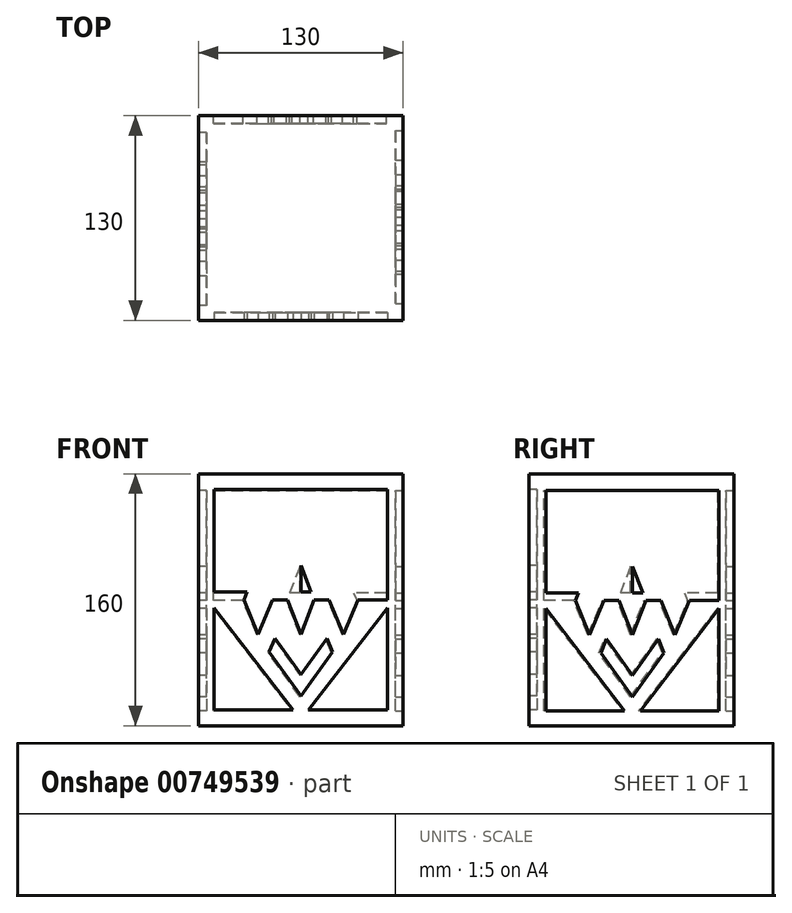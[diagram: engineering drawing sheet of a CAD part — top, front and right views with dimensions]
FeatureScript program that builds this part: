
annotation { "Feature Type Name" : "Feature", "Feature Type Description" : "" }
export const myFeature = defineFeature(function(context is Context, id is Id, definition is map)
    precondition{}
    {
        {
            var Q0;
            Q0=qCreatedBy(makeId("Top.planeOp"),FACE);
            var sketch = newSketch(context, id + "F0", { "sketchPlane" : qUnion([Q0])});
            skLineSegment(sketch, "E0.bottom", {"start": v(0, 0) * mm, "end": v(130, 0) * mm});
            skLineSegment(sketch, "E0.top", {"start": v(0, 130) * mm, "end": v(130, 130) * mm});
            skLineSegment(sketch, "E0.left", {"start": v(0, 0) * mm, "end": v(0, 130) * mm});
            skLineSegment(sketch, "E0.right", {"start": v(130, 0) * mm, "end": v(130, 130) * mm});
            skSolve(sketch);
        }
        {
            var Q0;
            Q0=makeQuery(id+"F0.imprint","IMPRINT",FACE,{"disambiguationData":[TD([[makeQuery(id+"F0.imprint","IMPRINT",EDGE,{"derivedFrom":sQuery(id+"F0.wireOp",EDGE,"E0.bottom")}),1.0]])]});
            extrude(context, id + "F1", {"entities" : qUnion([Q0]), "depth" : 160 * mm, "offsetDistance" : 25 * mm});
        }
        {
            var Q0;
            Q0=makeQuery(id+"F1.opExtrude","SWEPT_FACE",FACE,{"disambiguationData":[OSD([sQuery(id+"F0.wireOp",EDGE,"E0.bottom")])]});
            var sketch = newSketch(context, id + "F2", { "sketchPlane" : qUnion([Q0])});
            skLineSegment(sketch, "E1.0", {"start": v(10, 10) * mm, "end": v(120, 10) * mm});
            skLineSegment(sketch, "E1.1", {"start": v(10, 150) * mm, "end": v(10, 10) * mm});
            skLineSegment(sketch, "E1.2", {"start": v(120, 150) * mm, "end": v(10, 150) * mm});
            skLineSegment(sketch, "E1.3", {"start": v(120, 10) * mm, "end": v(120, 150) * mm});
            skLineSegment(sketch, "E2", {"start": v(10, 80) * mm, "end": v(120, 80) * mm});
            skLineSegment(sketch, "E3.0", {"start": v(10, 75) * mm, "end": v(120, 75) * mm});
            skLineSegment(sketch, "E4.0", {"start": v(10, 85) * mm, "end": v(120, 85) * mm});
            skLineSegment(sketch, "E5", {"start": v(10, 85) * mm, "end": v(60, 150) * mm});
            skLineSegment(sketch, "E6", {"start": v(65, 141.04) * mm, "end": v(44.9, 113.15) * mm});
            skLineSegment(sketch, "E7", {"start": v(44.9, 113.15) * mm, "end": v(48.52, 104.4) * mm});
            skLineSegment(sketch, "E8", {"start": v(48.52, 104.4) * mm, "end": v(65, 127.47) * mm});
            skLineSegment(sketch, "E9", {"start": v(47.01, 80) * mm, "end": v(28.77, 80) * mm});
            skLineSegment(sketch, "E10", {"start": v(37.89, 80) * mm, "end": v(37.89, 101.84) * mm});
            skLineSegment(sketch, "E11", {"start": v(37.89, 101.84) * mm, "end": v(28.77, 80) * mm});
            skLineSegment(sketch, "E12", {"start": v(37.89, 101.84) * mm, "end": v(47.01, 80) * mm});
            skLineSegment(sketch, "E13", {"start": v(65, 80) * mm, "end": v(65, 101.84) * mm});
            skLineSegment(sketch, "E14", {"start": v(65, 101.84) * mm, "end": v(56.51, 80) * mm});
            skLineSegment(sketch, "E15.MirrorCS", {"start": v(65, 141.04) * mm, "end": v(85.1, 113.15) * mm});
            skLineSegment(sketch, "E16.MirrorCS", {"start": v(81.48, 104.4) * mm, "end": v(65, 127.47) * mm});
            skLineSegment(sketch, "E17.MirrorCS", {"start": v(85.1, 113.15) * mm, "end": v(81.48, 104.4) * mm});
            skLineSegment(sketch, "E18.MirrorCS", {"start": v(120, 85) * mm, "end": v(70, 150) * mm});
            skLineSegment(sketch, "E19.MirrorCS", {"start": v(92.11, 101.84) * mm, "end": v(82.99, 80) * mm});
            skLineSegment(sketch, "E20.MirrorCS", {"start": v(92.11, 80) * mm, "end": v(92.11, 101.84) * mm});
            skLineSegment(sketch, "E21.MirrorCS", {"start": v(92.11, 101.84) * mm, "end": v(101.23, 80) * mm});
            skLineSegment(sketch, "E22.MirrorCS", {"start": v(65, 101.84) * mm, "end": v(73.49, 80) * mm});
            skLineSegment(sketch, "E23.MirrorCS", {"start": v(120, 75) * mm, "end": v(70, 10) * mm});
            skLineSegment(sketch, "E24.MirrorCS", {"start": v(92.11, 58.16) * mm, "end": v(101.23, 80) * mm});
            skLineSegment(sketch, "E25.MirrorCS", {"start": v(92.11, 80) * mm, "end": v(92.11, 58.16) * mm});
            skLineSegment(sketch, "E26.MirrorCS", {"start": v(92.11, 58.16) * mm, "end": v(82.99, 80) * mm});
            skLineSegment(sketch, "E27.MirrorCS", {"start": v(81.48, 55.6) * mm, "end": v(65, 32.53) * mm});
            skLineSegment(sketch, "E28.MirrorCS", {"start": v(85.1, 46.85) * mm, "end": v(81.48, 55.6) * mm});
            skLineSegment(sketch, "E29.MirrorCS", {"start": v(65, 18.96) * mm, "end": v(85.1, 46.85) * mm});
            skLineSegment(sketch, "E30.MirrorCS", {"start": v(65, 18.96) * mm, "end": v(44.9, 46.85) * mm});
            skLineSegment(sketch, "E31.MirrorCS", {"start": v(48.52, 55.6) * mm, "end": v(65, 32.53) * mm});
            skLineSegment(sketch, "E32.MirrorCS", {"start": v(44.9, 46.85) * mm, "end": v(48.52, 55.6) * mm});
            skLineSegment(sketch, "E33.MirrorCS", {"start": v(65, 58.16) * mm, "end": v(56.51, 80) * mm});
            skLineSegment(sketch, "E34.MirrorCS", {"start": v(65, 58.16) * mm, "end": v(73.49, 80) * mm});
            skLineSegment(sketch, "E35.MirrorCS", {"start": v(37.89, 58.16) * mm, "end": v(47.01, 80) * mm});
            skLineSegment(sketch, "E36.MirrorCS", {"start": v(37.89, 58.16) * mm, "end": v(28.77, 80) * mm});
            skLineSegment(sketch, "E37.MirrorCS", {"start": v(10, 75) * mm, "end": v(60, 10) * mm});
            skLineSegment(sketch, "E38", {"start": v(10, 150) * mm, "end": v(10, 85) * mm});
            skLineSegment(sketch, "E39", {"start": v(10, 150) * mm, "end": v(120, 150) * mm});
            skLineSegment(sketch, "E40", {"start": v(120, 150) * mm, "end": v(120, 10) * mm});
            skLineSegment(sketch, "E41", {"start": v(120, 10) * mm, "end": v(10, 10) * mm});
            skLineSegment(sketch, "E42", {"start": v(10, 10) * mm, "end": v(10, 75) * mm});
            skLineSegment(sketch, "E43.trimOffspring", {"start": v(60, 88.97) * mm, "end": v(60, 71.03) * mm});
            skLineSegment(sketch, "E44.trimOffspring", {"start": v(65, 101.84) * mm, "end": v(65, 58.16) * mm});
            skLineSegment(sketch, "E45.trimOffspring", {"start": v(65, 18.96) * mm, "end": v(65, 10) * mm});
            skPoint(sketch, "E46.start.orphan", {"position": v(65, 150) * mm});
            skSolve(sketch);
        }
        {
            var Q0;
            Q0=makeQuery(id+"F2.imprint","IMPRINT",FACE,{"disambiguationData":[TD([[makeQuery(id+"F2.imprint","IMPRINT",EDGE,{"derivedFrom":sQuery(id+"F2.wireOp",EDGE,"E6")}),1.0]])]});
            var Q1;
            Q1=makeQuery(id+"F2.imprint","IMPRINT",FACE,{"disambiguationData":[TD([[makeQuery(id+"F2.imprint","IMPRINT",EDGE,{"derivedFrom":sQuery(id+"F2.wireOp",EDGE,"E27.MirrorCS")}),1.0]])]});
            var Q2;
            {var subQ0=sQuery(id+"F2.wireOp",EDGE,"E23.MirrorCS");Q2=makeQuery(id+"F2.imprint","IMPRINT",FACE,{"disambiguationData":[TD([[makeQuery(id+"F2.imprint","IMPRINT",EDGE,{"derivedFrom":subQ0}),1.0]])]});}
            var Q3;
            {var subQ0=sQuery(id+"F2.wireOp",EDGE,"E37.MirrorCS");Q3=makeQuery(id+"F2.imprint","IMPRINT",FACE,{"disambiguationData":[TD([[makeQuery(id+"F2.imprint","IMPRINT",EDGE,{"derivedFrom":subQ0}),-1.0]])]});}
            var Q4;
            {var subQ0=sQuery(id+"F2.wireOp",EDGE,"E5");Q4=makeQuery(id+"F2.imprint","IMPRINT",FACE,{"disambiguationData":[TD([[makeQuery(id+"F2.imprint","IMPRINT",EDGE,{"derivedFrom":subQ0}),1.0]])]});}
            var Q5;
            {var subQ0=sQuery(id+"F2.wireOp",EDGE,"E18.MirrorCS");Q5=makeQuery(id+"F2.imprint","IMPRINT",FACE,{"disambiguationData":[TD([[makeQuery(id+"F2.imprint","IMPRINT",EDGE,{"derivedFrom":subQ0}),-1.0]])]});}
            var Q6;
            {var subQ0=sQuery(id+"F2.wireOp",EDGE,"E20.MirrorCS");var subQ1=sQuery(id+"F2.wireOp",EDGE,"E4.0");var subQ2=makeQuery(id+"F2.imprint","INTERSECT",VERTEX,{"derivedFrom":[subQ1,subQ0]});Q6=makeQuery(id+"F2.imprint","IMPRINT",FACE,{"disambiguationData":[TD([[makeQuery(id+"F2.imprint","IMPRINT",EDGE,{"disambiguationData":[TD([[subQ2,-1.0]])],"derivedFrom":subQ1}),1.0]])]});}
            var Q7;
            {var subQ0=sQuery(id+"F2.wireOp",EDGE,"E19.MirrorCS");var subQ1=sQuery(id+"F2.wireOp",EDGE,"E4.0");var subQ2=makeQuery(id+"F2.imprint","INTERSECT",VERTEX,{"derivedFrom":[subQ1,subQ0]});Q7=makeQuery(id+"F2.imprint","IMPRINT",FACE,{"disambiguationData":[TD([[makeQuery(id+"F2.imprint","IMPRINT",EDGE,{"disambiguationData":[TD([[subQ2,-1.0]])],"derivedFrom":subQ1}),1.0]])]});}
            var Q8;
            {var subQ0=sQuery(id+"F2.wireOp",EDGE,"E19.MirrorCS");var subQ5=sQuery(id+"F2.wireOp",EDGE,"E4.0");var subQ6=makeQuery(id+"F2.imprint","INTERSECT",VERTEX,{"derivedFrom":[subQ5,subQ0]});Q8=makeQuery(id+"F2.imprint","IMPRINT",FACE,{"disambiguationData":[TD([[makeQuery(id+"F2.imprint","IMPRINT",EDGE,{"disambiguationData":[TD([[subQ6,-1.0]])],"derivedFrom":subQ5}),-1.0]])]});}
            var Q9;
            {var subQ3=sQuery(id+"F2.wireOp",EDGE,"E20.MirrorCS");var subQ5=sQuery(id+"F2.wireOp",EDGE,"E4.0");var subQ7=makeQuery(id+"F2.imprint","INTERSECT",VERTEX,{"derivedFrom":[subQ5,subQ3]});Q9=makeQuery(id+"F2.imprint","IMPRINT",FACE,{"disambiguationData":[TD([[makeQuery(id+"F2.imprint","IMPRINT",EDGE,{"disambiguationData":[TD([[subQ7,-1.0]])],"derivedFrom":subQ5}),-1.0]])]});}
            var Q10;
            {var subQ3=sQuery(id+"F2.wireOp",EDGE,"E25.MirrorCS");var subQ5=sQuery(id+"F2.wireOp",EDGE,"E3.0");var subQ6=makeQuery(id+"F2.imprint","INTERSECT",VERTEX,{"derivedFrom":[subQ5,subQ3]});Q10=makeQuery(id+"F2.imprint","IMPRINT",FACE,{"disambiguationData":[TD([[makeQuery(id+"F2.imprint","IMPRINT",EDGE,{"disambiguationData":[TD([[subQ6,-1.0]])],"derivedFrom":subQ5}),1.0]])]});}
            var Q11;
            {var subQ0=sQuery(id+"F2.wireOp",EDGE,"E26.MirrorCS");var subQ5=sQuery(id+"F2.wireOp",EDGE,"E3.0");var subQ6=makeQuery(id+"F2.imprint","INTERSECT",VERTEX,{"derivedFrom":[subQ5,subQ0]});Q11=makeQuery(id+"F2.imprint","IMPRINT",FACE,{"disambiguationData":[TD([[makeQuery(id+"F2.imprint","IMPRINT",EDGE,{"disambiguationData":[TD([[subQ6,-1.0]])],"derivedFrom":subQ5}),1.0]])]});}
            var Q12;
            {var subQ0=sQuery(id+"F2.wireOp",EDGE,"E26.MirrorCS");var subQ1=sQuery(id+"F2.wireOp",EDGE,"E3.0");var subQ2=makeQuery(id+"F2.imprint","INTERSECT",VERTEX,{"derivedFrom":[subQ1,subQ0]});Q12=makeQuery(id+"F2.imprint","IMPRINT",FACE,{"disambiguationData":[TD([[makeQuery(id+"F2.imprint","IMPRINT",EDGE,{"disambiguationData":[TD([[subQ2,-1.0]])],"derivedFrom":subQ1}),-1.0]])]});}
            var Q13;
            {var subQ0=sQuery(id+"F2.wireOp",EDGE,"E25.MirrorCS");var subQ1=sQuery(id+"F2.wireOp",EDGE,"E3.0");var subQ2=makeQuery(id+"F2.imprint","INTERSECT",VERTEX,{"derivedFrom":[subQ1,subQ0]});Q13=makeQuery(id+"F2.imprint","IMPRINT",FACE,{"disambiguationData":[TD([[makeQuery(id+"F2.imprint","IMPRINT",EDGE,{"disambiguationData":[TD([[subQ2,-1.0]])],"derivedFrom":subQ1}),-1.0]])]});}
            var Q14;
            {var subQ0=sQuery(id+"F2.wireOp",EDGE,"E44.trimOffspring");var subQ1=sQuery(id+"F2.wireOp",EDGE,"E4.0");var subQ2=makeQuery(id+"F2.imprint","INTERSECT",VERTEX,{"derivedFrom":[subQ1,subQ0]});Q14=makeQuery(id+"F2.imprint","IMPRINT",FACE,{"disambiguationData":[TD([[makeQuery(id+"F2.imprint","IMPRINT",EDGE,{"disambiguationData":[TD([[subQ2,-1.0]])],"derivedFrom":subQ1}),1.0]])]});}
            var Q15;
            {var subQ0=sQuery(id+"F2.wireOp",EDGE,"E43.trimOffspring");var subQ1=sQuery(id+"F2.wireOp",EDGE,"E4.0");var subQ2=makeQuery(id+"F2.imprint","INTERSECT",VERTEX,{"derivedFrom":[subQ1,subQ0]});Q15=makeQuery(id+"F2.imprint","IMPRINT",FACE,{"disambiguationData":[TD([[makeQuery(id+"F2.imprint","IMPRINT",EDGE,{"disambiguationData":[TD([[subQ2,-1.0]])],"derivedFrom":subQ1}),1.0]])]});}
            var Q16;
            {var subQ0=sQuery(id+"F2.wireOp",EDGE,"E14");var subQ1=sQuery(id+"F2.wireOp",EDGE,"E4.0");var subQ2=makeQuery(id+"F2.imprint","INTERSECT",VERTEX,{"derivedFrom":[subQ1,subQ0]});Q16=makeQuery(id+"F2.imprint","IMPRINT",FACE,{"disambiguationData":[TD([[makeQuery(id+"F2.imprint","IMPRINT",EDGE,{"disambiguationData":[TD([[subQ2,-1.0]])],"derivedFrom":subQ1}),1.0]])]});}
            var Q17;
            {var subQ0=sQuery(id+"F2.wireOp",EDGE,"E14");var subQ5=sQuery(id+"F2.wireOp",EDGE,"E4.0");var subQ6=makeQuery(id+"F2.imprint","INTERSECT",VERTEX,{"derivedFrom":[subQ5,subQ0]});Q17=makeQuery(id+"F2.imprint","IMPRINT",FACE,{"disambiguationData":[TD([[makeQuery(id+"F2.imprint","IMPRINT",EDGE,{"disambiguationData":[TD([[subQ6,-1.0]])],"derivedFrom":subQ5}),-1.0]])]});}
            var Q18;
            {var subQ0=sQuery(id+"F2.wireOp",EDGE,"E33.MirrorCS");var subQ5=sQuery(id+"F2.wireOp",EDGE,"E3.0");var subQ6=makeQuery(id+"F2.imprint","INTERSECT",VERTEX,{"derivedFrom":[subQ5,subQ0]});Q18=makeQuery(id+"F2.imprint","IMPRINT",FACE,{"disambiguationData":[TD([[makeQuery(id+"F2.imprint","IMPRINT",EDGE,{"disambiguationData":[TD([[subQ6,-1.0]])],"derivedFrom":subQ5}),1.0]])]});}
            var Q19;
            {var subQ0=sQuery(id+"F2.wireOp",EDGE,"E43.trimOffspring");var subQ1=sQuery(id+"F2.wireOp",EDGE,"E2");var subQ2=makeQuery(id+"F2.imprint","INTERSECT",VERTEX,{"derivedFrom":[subQ1,subQ0]});Q19=makeQuery(id+"F2.imprint","IMPRINT",FACE,{"disambiguationData":[TD([[makeQuery(id+"F2.imprint","IMPRINT",EDGE,{"disambiguationData":[TD([[subQ2,-1.0]])],"derivedFrom":subQ1}),1.0]])]});}
            var Q20;
            {var subQ0=sQuery(id+"F2.wireOp",EDGE,"E43.trimOffspring");var subQ1=sQuery(id+"F2.wireOp",EDGE,"E2");var subQ2=makeQuery(id+"F2.imprint","INTERSECT",VERTEX,{"derivedFrom":[subQ1,subQ0]});Q20=makeQuery(id+"F2.imprint","IMPRINT",FACE,{"disambiguationData":[TD([[makeQuery(id+"F2.imprint","IMPRINT",EDGE,{"disambiguationData":[TD([[subQ2,-1.0]])],"derivedFrom":subQ1}),-1.0]])]});}
            var Q21;
            {var subQ0=sQuery(id+"F2.wireOp",EDGE,"E43.trimOffspring");var subQ1=sQuery(id+"F2.wireOp",EDGE,"E3.0");var subQ2=makeQuery(id+"F2.imprint","INTERSECT",VERTEX,{"derivedFrom":[subQ1,subQ0]});Q21=makeQuery(id+"F2.imprint","IMPRINT",FACE,{"disambiguationData":[TD([[makeQuery(id+"F2.imprint","IMPRINT",EDGE,{"disambiguationData":[TD([[subQ2,-1.0]])],"derivedFrom":subQ1}),-1.0]])]});}
            var Q22;
            {var subQ0=sQuery(id+"F2.wireOp",EDGE,"E44.trimOffspring");var subQ1=sQuery(id+"F2.wireOp",EDGE,"E3.0");var subQ2=makeQuery(id+"F2.imprint","INTERSECT",VERTEX,{"derivedFrom":[subQ1,subQ0]});Q22=makeQuery(id+"F2.imprint","IMPRINT",FACE,{"disambiguationData":[TD([[makeQuery(id+"F2.imprint","IMPRINT",EDGE,{"disambiguationData":[TD([[subQ2,-1.0]])],"derivedFrom":subQ1}),-1.0]])]});}
            var Q23;
            {var subQ3=sQuery(id+"F2.wireOp",EDGE,"E44.trimOffspring");var subQ5=sQuery(id+"F2.wireOp",EDGE,"E3.0");var subQ6=makeQuery(id+"F2.imprint","INTERSECT",VERTEX,{"derivedFrom":[subQ5,subQ3]});Q23=makeQuery(id+"F2.imprint","IMPRINT",FACE,{"disambiguationData":[TD([[makeQuery(id+"F2.imprint","IMPRINT",EDGE,{"disambiguationData":[TD([[subQ6,-1.0]])],"derivedFrom":subQ5}),1.0]])]});}
            var Q24;
            {var subQ3=sQuery(id+"F2.wireOp",EDGE,"E44.trimOffspring");var subQ5=sQuery(id+"F2.wireOp",EDGE,"E4.0");var subQ6=makeQuery(id+"F2.imprint","INTERSECT",VERTEX,{"derivedFrom":[subQ5,subQ3]});Q24=makeQuery(id+"F2.imprint","IMPRINT",FACE,{"disambiguationData":[TD([[makeQuery(id+"F2.imprint","IMPRINT",EDGE,{"disambiguationData":[TD([[subQ6,-1.0]])],"derivedFrom":subQ5}),-1.0]])]});}
            var Q25;
            {var subQ0=sQuery(id+"F2.wireOp",EDGE,"E10");var subQ1=sQuery(id+"F2.wireOp",EDGE,"E4.0");var subQ2=makeQuery(id+"F2.imprint","INTERSECT",VERTEX,{"derivedFrom":[subQ1,subQ0]});Q25=makeQuery(id+"F2.imprint","IMPRINT",FACE,{"disambiguationData":[TD([[makeQuery(id+"F2.imprint","IMPRINT",EDGE,{"disambiguationData":[TD([[subQ2,-1.0]])],"derivedFrom":subQ1}),1.0]])]});}
            var Q26;
            {var subQ0=sQuery(id+"F2.wireOp",EDGE,"E11");var subQ1=sQuery(id+"F2.wireOp",EDGE,"E4.0");var subQ2=makeQuery(id+"F2.imprint","INTERSECT",VERTEX,{"derivedFrom":[subQ1,subQ0]});Q26=makeQuery(id+"F2.imprint","IMPRINT",FACE,{"disambiguationData":[TD([[makeQuery(id+"F2.imprint","IMPRINT",EDGE,{"disambiguationData":[TD([[subQ2,-1.0]])],"derivedFrom":subQ1}),1.0]])]});}
            var Q27;
            {var subQ0=sQuery(id+"F2.wireOp",EDGE,"E11");var subQ1=sQuery(id+"F2.wireOp",EDGE,"E4.0");var subQ2=makeQuery(id+"F2.imprint","INTERSECT",VERTEX,{"derivedFrom":[subQ1,subQ0]});Q27=makeQuery(id+"F2.imprint","IMPRINT",FACE,{"disambiguationData":[TD([[makeQuery(id+"F2.imprint","IMPRINT",EDGE,{"disambiguationData":[TD([[subQ2,-1.0]])],"derivedFrom":subQ1}),-1.0]])]});}
            var Q28;
            {var subQ0=sQuery(id+"F2.wireOp",EDGE,"E10");var subQ1=sQuery(id+"F2.wireOp",EDGE,"E4.0");var subQ2=makeQuery(id+"F2.imprint","INTERSECT",VERTEX,{"derivedFrom":[subQ1,subQ0]});Q28=makeQuery(id+"F2.imprint","IMPRINT",FACE,{"disambiguationData":[TD([[makeQuery(id+"F2.imprint","IMPRINT",EDGE,{"disambiguationData":[TD([[subQ2,-1.0]])],"derivedFrom":subQ1}),-1.0]])]});}
            var Q29;
            {var subQ4=sQuery(id+"F2.wireOp",EDGE,"E3.0");var subQ6=sQuery(id+"F2.wireOp",EDGE,"E36.MirrorCS");var subQ7=makeQuery(id+"F2.imprint","INTERSECT",VERTEX,{"derivedFrom":[subQ4,subQ6]});Q29=makeQuery(id+"F2.imprint","IMPRINT",FACE,{"disambiguationData":[TD([[makeQuery(id+"F2.imprint","IMPRINT",EDGE,{"disambiguationData":[TD([[subQ7,-1.0]])],"derivedFrom":subQ4}),1.0]])]});}
            var Q30;
            {var subQ0=sQuery(id+"F2.wireOp",EDGE,"E36.MirrorCS");var subQ1=sQuery(id+"F2.wireOp",EDGE,"E3.0");var subQ2=makeQuery(id+"F2.imprint","INTERSECT",VERTEX,{"derivedFrom":[subQ1,subQ0]});Q30=makeQuery(id+"F2.imprint","IMPRINT",FACE,{"disambiguationData":[TD([[makeQuery(id+"F2.imprint","IMPRINT",EDGE,{"disambiguationData":[TD([[subQ2,-1.0]])],"derivedFrom":subQ1}),-1.0]])]});}
            var Q31;
            {var subQ0=sQuery(id+"F2.wireOp",EDGE,"E33.MirrorCS");var subQ1=sQuery(id+"F2.wireOp",EDGE,"E3.0");var subQ2=makeQuery(id+"F2.imprint","INTERSECT",VERTEX,{"derivedFrom":[subQ1,subQ0]});Q31=makeQuery(id+"F2.imprint","IMPRINT",FACE,{"disambiguationData":[TD([[makeQuery(id+"F2.imprint","IMPRINT",EDGE,{"disambiguationData":[TD([[subQ2,-1.0]])],"derivedFrom":subQ1}),-1.0]])]});}
            extrude(context, id + "F3", {"entities" : qUnion([Q0, Q1, Q2, Q3, Q4, Q5, Q6, Q7, Q8, Q9, Q10, Q11, Q12, Q13, Q14, Q15, Q16, Q17, Q18, Q19, Q20, Q21, Q22, Q23, Q24, Q25, Q26, Q27, Q28, Q29, Q30, Q31]), "operationType" : NewBodyOperationType.REMOVE, "oppositeDirection" : true, "depth" : 5 * mm, "offsetDistance" : 25 * mm});
        }
        {
            var Q0;
            Q0=makeQuery(id+"F1.opExtrude","SWEPT_FACE",FACE,{"disambiguationData":[OSD([sQuery(id+"F0.wireOp",EDGE,"E0.right")])]});
            var sketch = newSketch(context, id + "F4", { "sketchPlane" : qUnion([Q0])});
            skLineSegment(sketch, "E47.0", {"start": v(10.56, 9.48) * mm, "end": v(120.56, 9.48) * mm});
            skLineSegment(sketch, "E47.1", {"start": v(10.56, 149.48) * mm, "end": v(10.56, 9.48) * mm});
            skLineSegment(sketch, "E47.2", {"start": v(120.56, 149.48) * mm, "end": v(10.56, 149.48) * mm});
            skLineSegment(sketch, "E47.3", {"start": v(120.56, 9.48) * mm, "end": v(120.56, 149.48) * mm});
            skLineSegment(sketch, "E48", {"start": v(10.56, 79.48) * mm, "end": v(120.56, 79.48) * mm});
            skLineSegment(sketch, "E49.0", {"start": v(10.56, 74.48) * mm, "end": v(120.56, 74.48) * mm});
            skLineSegment(sketch, "E50.0", {"start": v(10.56, 84.48) * mm, "end": v(120.56, 84.48) * mm});
            skLineSegment(sketch, "E51", {"start": v(10.56, 84.48) * mm, "end": v(60.56, 149.48) * mm});
            skLineSegment(sketch, "E52", {"start": v(65.56, 140.53) * mm, "end": v(45.46, 112.63) * mm});
            skLineSegment(sketch, "E53", {"start": v(45.46, 112.63) * mm, "end": v(49.08, 103.88) * mm});
            skLineSegment(sketch, "E54", {"start": v(49.08, 103.88) * mm, "end": v(65.56, 126.95) * mm});
            skLineSegment(sketch, "E55", {"start": v(47.57, 79.48) * mm, "end": v(29.33, 79.48) * mm});
            skLineSegment(sketch, "E56", {"start": v(38.45, 79.48) * mm, "end": v(38.45, 101.32) * mm});
            skLineSegment(sketch, "E57", {"start": v(38.45, 101.32) * mm, "end": v(29.33, 79.48) * mm});
            skLineSegment(sketch, "E58", {"start": v(38.45, 101.32) * mm, "end": v(47.57, 79.48) * mm});
            skLineSegment(sketch, "E59", {"start": v(65.56, 79.48) * mm, "end": v(65.56, 101.32) * mm});
            skLineSegment(sketch, "E60", {"start": v(65.56, 101.32) * mm, "end": v(57.07, 79.48) * mm});
            skLineSegment(sketch, "E61.MirrorCS", {"start": v(65.56, 140.53) * mm, "end": v(85.66, 112.63) * mm});
            skLineSegment(sketch, "E62.MirrorCS", {"start": v(82.04, 103.88) * mm, "end": v(65.56, 126.95) * mm});
            skLineSegment(sketch, "E63.MirrorCS", {"start": v(85.66, 112.63) * mm, "end": v(82.04, 103.88) * mm});
            skLineSegment(sketch, "E64.MirrorCS", {"start": v(120.56, 84.48) * mm, "end": v(70.56, 149.48) * mm});
            skLineSegment(sketch, "E65.MirrorCS", {"start": v(92.67, 101.32) * mm, "end": v(83.55, 79.48) * mm});
            skLineSegment(sketch, "E66.MirrorCS", {"start": v(92.67, 79.48) * mm, "end": v(92.67, 101.32) * mm});
            skLineSegment(sketch, "E67.MirrorCS", {"start": v(92.67, 101.32) * mm, "end": v(101.8, 79.48) * mm});
            skLineSegment(sketch, "E68.MirrorCS", {"start": v(65.56, 101.32) * mm, "end": v(74.05, 79.48) * mm});
            skLineSegment(sketch, "E69.MirrorCS", {"start": v(120.56, 74.48) * mm, "end": v(70.56, 9.48) * mm});
            skLineSegment(sketch, "E70.MirrorCS", {"start": v(92.67, 57.65) * mm, "end": v(101.8, 79.48) * mm});
            skLineSegment(sketch, "E71.MirrorCS", {"start": v(92.67, 79.48) * mm, "end": v(92.67, 57.65) * mm});
            skLineSegment(sketch, "E72.MirrorCS", {"start": v(92.67, 57.65) * mm, "end": v(83.55, 79.48) * mm});
            skLineSegment(sketch, "E73.MirrorCS", {"start": v(82.04, 55.08) * mm, "end": v(65.56, 32.01) * mm});
            skLineSegment(sketch, "E74.MirrorCS", {"start": v(85.66, 46.34) * mm, "end": v(82.04, 55.08) * mm});
            skLineSegment(sketch, "E75.MirrorCS", {"start": v(65.56, 18.44) * mm, "end": v(85.66, 46.34) * mm});
            skLineSegment(sketch, "E76.MirrorCS", {"start": v(65.56, 18.44) * mm, "end": v(45.46, 46.34) * mm});
            skLineSegment(sketch, "E77.MirrorCS", {"start": v(49.08, 55.08) * mm, "end": v(65.56, 32.01) * mm});
            skLineSegment(sketch, "E78.MirrorCS", {"start": v(45.46, 46.34) * mm, "end": v(49.08, 55.08) * mm});
            skLineSegment(sketch, "E79.MirrorCS", {"start": v(65.56, 57.65) * mm, "end": v(57.07, 79.48) * mm});
            skLineSegment(sketch, "E80.MirrorCS", {"start": v(65.56, 57.65) * mm, "end": v(74.05, 79.48) * mm});
            skLineSegment(sketch, "E81.MirrorCS", {"start": v(38.45, 57.65) * mm, "end": v(47.57, 79.48) * mm});
            skLineSegment(sketch, "E82.MirrorCS", {"start": v(38.45, 57.65) * mm, "end": v(29.33, 79.48) * mm});
            skLineSegment(sketch, "E83.MirrorCS", {"start": v(10.56, 74.48) * mm, "end": v(60.56, 9.48) * mm});
            skLineSegment(sketch, "E84", {"start": v(10.56, 149.48) * mm, "end": v(10.56, 84.48) * mm});
            skLineSegment(sketch, "E85", {"start": v(10.56, 149.48) * mm, "end": v(120.56, 149.48) * mm});
            skLineSegment(sketch, "E86", {"start": v(120.56, 149.48) * mm, "end": v(120.56, 9.48) * mm});
            skLineSegment(sketch, "E87", {"start": v(120.56, 9.48) * mm, "end": v(10.56, 9.48) * mm});
            skLineSegment(sketch, "E88", {"start": v(10.56, 9.48) * mm, "end": v(10.56, 74.48) * mm});
            skLineSegment(sketch, "E89.trimOffspring", {"start": v(60.56, 88.46) * mm, "end": v(60.56, 70.5) * mm});
            skLineSegment(sketch, "E90.trimOffspring", {"start": v(65.56, 101.32) * mm, "end": v(65.56, 57.65) * mm});
            skLineSegment(sketch, "E91.trimOffspring", {"start": v(65.56, 18.44) * mm, "end": v(65.56, 9.48) * mm});
            skPoint(sketch, "E92.start.orphan", {"position": v(65.56, 149.48) * mm});
            skSolve(sketch);
        }
        {
            var Q0;
            Q0=makeQuery(id+"F4.imprint","IMPRINT",FACE,{"disambiguationData":[TD([[makeQuery(id+"F4.imprint","IMPRINT",EDGE,{"derivedFrom":sQuery(id+"F4.wireOp",EDGE,"E52")}),1.0]])]});
            var Q1;
            {var subQ0=sQuery(id+"F4.wireOp",EDGE,"E65.MirrorCS");var subQ1=sQuery(id+"F4.wireOp",EDGE,"E50.0");var subQ2=makeQuery(id+"F4.imprint","INTERSECT",VERTEX,{"derivedFrom":[subQ1,subQ0]});Q1=makeQuery(id+"F4.imprint","IMPRINT",FACE,{"disambiguationData":[TD([[makeQuery(id+"F4.imprint","IMPRINT",EDGE,{"disambiguationData":[TD([[subQ2,-1.0]])],"derivedFrom":subQ1}),1.0]])]});}
            var Q2;
            {var subQ0=sQuery(id+"F4.wireOp",EDGE,"E66.MirrorCS");var subQ1=sQuery(id+"F4.wireOp",EDGE,"E50.0");var subQ2=makeQuery(id+"F4.imprint","INTERSECT",VERTEX,{"derivedFrom":[subQ1,subQ0]});Q2=makeQuery(id+"F4.imprint","IMPRINT",FACE,{"disambiguationData":[TD([[makeQuery(id+"F4.imprint","IMPRINT",EDGE,{"disambiguationData":[TD([[subQ2,-1.0]])],"derivedFrom":subQ1}),1.0]])]});}
            var Q3;
            {var subQ3=sQuery(id+"F4.wireOp",EDGE,"E66.MirrorCS");var subQ5=sQuery(id+"F4.wireOp",EDGE,"E50.0");var subQ7=makeQuery(id+"F4.imprint","INTERSECT",VERTEX,{"derivedFrom":[subQ5,subQ3]});Q3=makeQuery(id+"F4.imprint","IMPRINT",FACE,{"disambiguationData":[TD([[makeQuery(id+"F4.imprint","IMPRINT",EDGE,{"disambiguationData":[TD([[subQ7,-1.0]])],"derivedFrom":subQ5}),-1.0]])]});}
            var Q4;
            {var subQ0=sQuery(id+"F4.wireOp",EDGE,"E65.MirrorCS");var subQ5=sQuery(id+"F4.wireOp",EDGE,"E50.0");var subQ6=makeQuery(id+"F4.imprint","INTERSECT",VERTEX,{"derivedFrom":[subQ5,subQ0]});Q4=makeQuery(id+"F4.imprint","IMPRINT",FACE,{"disambiguationData":[TD([[makeQuery(id+"F4.imprint","IMPRINT",EDGE,{"disambiguationData":[TD([[subQ6,-1.0]])],"derivedFrom":subQ5}),-1.0]])]});}
            var Q5;
            {var subQ0=sQuery(id+"F4.wireOp",EDGE,"E72.MirrorCS");var subQ5=sQuery(id+"F4.wireOp",EDGE,"E49.0");var subQ6=makeQuery(id+"F4.imprint","INTERSECT",VERTEX,{"derivedFrom":[subQ5,subQ0]});Q5=makeQuery(id+"F4.imprint","IMPRINT",FACE,{"disambiguationData":[TD([[makeQuery(id+"F4.imprint","IMPRINT",EDGE,{"disambiguationData":[TD([[subQ6,-1.0]])],"derivedFrom":subQ5}),1.0]])]});}
            var Q6;
            {var subQ3=sQuery(id+"F4.wireOp",EDGE,"E71.MirrorCS");var subQ5=sQuery(id+"F4.wireOp",EDGE,"E49.0");var subQ6=makeQuery(id+"F4.imprint","INTERSECT",VERTEX,{"derivedFrom":[subQ5,subQ3]});Q6=makeQuery(id+"F4.imprint","IMPRINT",FACE,{"disambiguationData":[TD([[makeQuery(id+"F4.imprint","IMPRINT",EDGE,{"disambiguationData":[TD([[subQ6,-1.0]])],"derivedFrom":subQ5}),1.0]])]});}
            var Q7;
            {var subQ0=sQuery(id+"F4.wireOp",EDGE,"E71.MirrorCS");var subQ1=sQuery(id+"F4.wireOp",EDGE,"E49.0");var subQ2=makeQuery(id+"F4.imprint","INTERSECT",VERTEX,{"derivedFrom":[subQ1,subQ0]});Q7=makeQuery(id+"F4.imprint","IMPRINT",FACE,{"disambiguationData":[TD([[makeQuery(id+"F4.imprint","IMPRINT",EDGE,{"disambiguationData":[TD([[subQ2,-1.0]])],"derivedFrom":subQ1}),-1.0]])]});}
            var Q8;
            {var subQ0=sQuery(id+"F4.wireOp",EDGE,"E72.MirrorCS");var subQ1=sQuery(id+"F4.wireOp",EDGE,"E49.0");var subQ2=makeQuery(id+"F4.imprint","INTERSECT",VERTEX,{"derivedFrom":[subQ1,subQ0]});Q8=makeQuery(id+"F4.imprint","IMPRINT",FACE,{"disambiguationData":[TD([[makeQuery(id+"F4.imprint","IMPRINT",EDGE,{"disambiguationData":[TD([[subQ2,-1.0]])],"derivedFrom":subQ1}),-1.0]])]});}
            var Q9;
            {var subQ0=sQuery(id+"F4.wireOp",EDGE,"E90.trimOffspring");var subQ1=sQuery(id+"F4.wireOp",EDGE,"E50.0");var subQ2=makeQuery(id+"F4.imprint","INTERSECT",VERTEX,{"derivedFrom":[subQ1,subQ0]});Q9=makeQuery(id+"F4.imprint","IMPRINT",FACE,{"disambiguationData":[TD([[makeQuery(id+"F4.imprint","IMPRINT",EDGE,{"disambiguationData":[TD([[subQ2,-1.0]])],"derivedFrom":subQ1}),1.0]])]});}
            var Q10;
            {var subQ0=sQuery(id+"F4.wireOp",EDGE,"E89.trimOffspring");var subQ1=sQuery(id+"F4.wireOp",EDGE,"E50.0");var subQ2=makeQuery(id+"F4.imprint","INTERSECT",VERTEX,{"derivedFrom":[subQ1,subQ0]});Q10=makeQuery(id+"F4.imprint","IMPRINT",FACE,{"disambiguationData":[TD([[makeQuery(id+"F4.imprint","IMPRINT",EDGE,{"disambiguationData":[TD([[subQ2,-1.0]])],"derivedFrom":subQ1}),1.0]])]});}
            var Q11;
            {var subQ0=sQuery(id+"F4.wireOp",EDGE,"E60");var subQ1=sQuery(id+"F4.wireOp",EDGE,"E50.0");var subQ2=makeQuery(id+"F4.imprint","INTERSECT",VERTEX,{"derivedFrom":[subQ1,subQ0]});Q11=makeQuery(id+"F4.imprint","IMPRINT",FACE,{"disambiguationData":[TD([[makeQuery(id+"F4.imprint","IMPRINT",EDGE,{"disambiguationData":[TD([[subQ2,-1.0]])],"derivedFrom":subQ1}),1.0]])]});}
            var Q12;
            {var subQ0=sQuery(id+"F4.wireOp",EDGE,"E60");var subQ5=sQuery(id+"F4.wireOp",EDGE,"E50.0");var subQ6=makeQuery(id+"F4.imprint","INTERSECT",VERTEX,{"derivedFrom":[subQ5,subQ0]});Q12=makeQuery(id+"F4.imprint","IMPRINT",FACE,{"disambiguationData":[TD([[makeQuery(id+"F4.imprint","IMPRINT",EDGE,{"disambiguationData":[TD([[subQ6,-1.0]])],"derivedFrom":subQ5}),-1.0]])]});}
            var Q13;
            {var subQ0=sQuery(id+"F4.wireOp",EDGE,"E89.trimOffspring");var subQ1=sQuery(id+"F4.wireOp",EDGE,"E48");var subQ2=makeQuery(id+"F4.imprint","INTERSECT",VERTEX,{"derivedFrom":[subQ1,subQ0]});Q13=makeQuery(id+"F4.imprint","IMPRINT",FACE,{"disambiguationData":[TD([[makeQuery(id+"F4.imprint","IMPRINT",EDGE,{"disambiguationData":[TD([[subQ2,-1.0]])],"derivedFrom":subQ1}),1.0]])]});}
            var Q14;
            {var subQ3=sQuery(id+"F4.wireOp",EDGE,"E90.trimOffspring");var subQ5=sQuery(id+"F4.wireOp",EDGE,"E50.0");var subQ6=makeQuery(id+"F4.imprint","INTERSECT",VERTEX,{"derivedFrom":[subQ5,subQ3]});Q14=makeQuery(id+"F4.imprint","IMPRINT",FACE,{"disambiguationData":[TD([[makeQuery(id+"F4.imprint","IMPRINT",EDGE,{"disambiguationData":[TD([[subQ6,-1.0]])],"derivedFrom":subQ5}),-1.0]])]});}
            var Q15;
            {var subQ3=sQuery(id+"F4.wireOp",EDGE,"E90.trimOffspring");var subQ5=sQuery(id+"F4.wireOp",EDGE,"E49.0");var subQ6=makeQuery(id+"F4.imprint","INTERSECT",VERTEX,{"derivedFrom":[subQ5,subQ3]});Q15=makeQuery(id+"F4.imprint","IMPRINT",FACE,{"disambiguationData":[TD([[makeQuery(id+"F4.imprint","IMPRINT",EDGE,{"disambiguationData":[TD([[subQ6,-1.0]])],"derivedFrom":subQ5}),1.0]])]});}
            var Q16;
            {var subQ0=sQuery(id+"F4.wireOp",EDGE,"E89.trimOffspring");var subQ1=sQuery(id+"F4.wireOp",EDGE,"E48");var subQ2=makeQuery(id+"F4.imprint","INTERSECT",VERTEX,{"derivedFrom":[subQ1,subQ0]});Q16=makeQuery(id+"F4.imprint","IMPRINT",FACE,{"disambiguationData":[TD([[makeQuery(id+"F4.imprint","IMPRINT",EDGE,{"disambiguationData":[TD([[subQ2,-1.0]])],"derivedFrom":subQ1}),-1.0]])]});}
            var Q17;
            {var subQ0=sQuery(id+"F4.wireOp",EDGE,"E79.MirrorCS");var subQ5=sQuery(id+"F4.wireOp",EDGE,"E49.0");var subQ6=makeQuery(id+"F4.imprint","INTERSECT",VERTEX,{"derivedFrom":[subQ5,subQ0]});Q17=makeQuery(id+"F4.imprint","IMPRINT",FACE,{"disambiguationData":[TD([[makeQuery(id+"F4.imprint","IMPRINT",EDGE,{"disambiguationData":[TD([[subQ6,-1.0]])],"derivedFrom":subQ5}),1.0]])]});}
            var Q18;
            {var subQ0=sQuery(id+"F4.wireOp",EDGE,"E79.MirrorCS");var subQ1=sQuery(id+"F4.wireOp",EDGE,"E49.0");var subQ2=makeQuery(id+"F4.imprint","INTERSECT",VERTEX,{"derivedFrom":[subQ1,subQ0]});Q18=makeQuery(id+"F4.imprint","IMPRINT",FACE,{"disambiguationData":[TD([[makeQuery(id+"F4.imprint","IMPRINT",EDGE,{"disambiguationData":[TD([[subQ2,-1.0]])],"derivedFrom":subQ1}),-1.0]])]});}
            var Q19;
            {var subQ0=sQuery(id+"F4.wireOp",EDGE,"E89.trimOffspring");var subQ1=sQuery(id+"F4.wireOp",EDGE,"E49.0");var subQ2=makeQuery(id+"F4.imprint","INTERSECT",VERTEX,{"derivedFrom":[subQ1,subQ0]});Q19=makeQuery(id+"F4.imprint","IMPRINT",FACE,{"disambiguationData":[TD([[makeQuery(id+"F4.imprint","IMPRINT",EDGE,{"disambiguationData":[TD([[subQ2,-1.0]])],"derivedFrom":subQ1}),-1.0]])]});}
            var Q20;
            {var subQ0=sQuery(id+"F4.wireOp",EDGE,"E90.trimOffspring");var subQ1=sQuery(id+"F4.wireOp",EDGE,"E49.0");var subQ2=makeQuery(id+"F4.imprint","INTERSECT",VERTEX,{"derivedFrom":[subQ1,subQ0]});Q20=makeQuery(id+"F4.imprint","IMPRINT",FACE,{"disambiguationData":[TD([[makeQuery(id+"F4.imprint","IMPRINT",EDGE,{"disambiguationData":[TD([[subQ2,-1.0]])],"derivedFrom":subQ1}),-1.0]])]});}
            var Q21;
            {var subQ0=sQuery(id+"F4.wireOp",EDGE,"E56");var subQ1=sQuery(id+"F4.wireOp",EDGE,"E50.0");var subQ2=makeQuery(id+"F4.imprint","INTERSECT",VERTEX,{"derivedFrom":[subQ1,subQ0]});Q21=makeQuery(id+"F4.imprint","IMPRINT",FACE,{"disambiguationData":[TD([[makeQuery(id+"F4.imprint","IMPRINT",EDGE,{"disambiguationData":[TD([[subQ2,-1.0]])],"derivedFrom":subQ1}),1.0]])]});}
            var Q22;
            {var subQ0=sQuery(id+"F4.wireOp",EDGE,"E57");var subQ1=sQuery(id+"F4.wireOp",EDGE,"E50.0");var subQ2=makeQuery(id+"F4.imprint","INTERSECT",VERTEX,{"derivedFrom":[subQ1,subQ0]});Q22=makeQuery(id+"F4.imprint","IMPRINT",FACE,{"disambiguationData":[TD([[makeQuery(id+"F4.imprint","IMPRINT",EDGE,{"disambiguationData":[TD([[subQ2,-1.0]])],"derivedFrom":subQ1}),1.0]])]});}
            var Q23;
            {var subQ0=sQuery(id+"F4.wireOp",EDGE,"E57");var subQ1=sQuery(id+"F4.wireOp",EDGE,"E50.0");var subQ2=makeQuery(id+"F4.imprint","INTERSECT",VERTEX,{"derivedFrom":[subQ1,subQ0]});Q23=makeQuery(id+"F4.imprint","IMPRINT",FACE,{"disambiguationData":[TD([[makeQuery(id+"F4.imprint","IMPRINT",EDGE,{"disambiguationData":[TD([[subQ2,-1.0]])],"derivedFrom":subQ1}),-1.0]])]});}
            var Q24;
            {var subQ0=sQuery(id+"F4.wireOp",EDGE,"E56");var subQ1=sQuery(id+"F4.wireOp",EDGE,"E50.0");var subQ2=makeQuery(id+"F4.imprint","INTERSECT",VERTEX,{"derivedFrom":[subQ1,subQ0]});Q24=makeQuery(id+"F4.imprint","IMPRINT",FACE,{"disambiguationData":[TD([[makeQuery(id+"F4.imprint","IMPRINT",EDGE,{"disambiguationData":[TD([[subQ2,-1.0]])],"derivedFrom":subQ1}),-1.0]])]});}
            var Q25;
            {var subQ4=sQuery(id+"F4.wireOp",EDGE,"E49.0");var subQ6=sQuery(id+"F4.wireOp",EDGE,"E82.MirrorCS");var subQ7=makeQuery(id+"F4.imprint","INTERSECT",VERTEX,{"derivedFrom":[subQ4,subQ6]});Q25=makeQuery(id+"F4.imprint","IMPRINT",FACE,{"disambiguationData":[TD([[makeQuery(id+"F4.imprint","IMPRINT",EDGE,{"disambiguationData":[TD([[subQ7,-1.0]])],"derivedFrom":subQ4}),1.0]])]});}
            var Q26;
            {var subQ0=sQuery(id+"F4.wireOp",EDGE,"E82.MirrorCS");var subQ1=sQuery(id+"F4.wireOp",EDGE,"E49.0");var subQ2=makeQuery(id+"F4.imprint","INTERSECT",VERTEX,{"derivedFrom":[subQ1,subQ0]});Q26=makeQuery(id+"F4.imprint","IMPRINT",FACE,{"disambiguationData":[TD([[makeQuery(id+"F4.imprint","IMPRINT",EDGE,{"disambiguationData":[TD([[subQ2,-1.0]])],"derivedFrom":subQ1}),-1.0]])]});}
            var Q27;
            Q27=makeQuery(id+"F4.imprint","IMPRINT",FACE,{"disambiguationData":[TD([[makeQuery(id+"F4.imprint","IMPRINT",EDGE,{"derivedFrom":sQuery(id+"F4.wireOp",EDGE,"E73.MirrorCS")}),1.0]])]});
            var Q28;
            {var subQ0=sQuery(id+"F4.wireOp",EDGE,"E83.MirrorCS");Q28=makeQuery(id+"F4.imprint","IMPRINT",FACE,{"disambiguationData":[TD([[makeQuery(id+"F4.imprint","IMPRINT",EDGE,{"derivedFrom":subQ0}),-1.0]])]});}
            var Q29;
            {var subQ0=sQuery(id+"F4.wireOp",EDGE,"E69.MirrorCS");Q29=makeQuery(id+"F4.imprint","IMPRINT",FACE,{"disambiguationData":[TD([[makeQuery(id+"F4.imprint","IMPRINT",EDGE,{"derivedFrom":subQ0}),1.0]])]});}
            var Q30;
            {var subQ0=sQuery(id+"F4.wireOp",EDGE,"E64.MirrorCS");Q30=makeQuery(id+"F4.imprint","IMPRINT",FACE,{"disambiguationData":[TD([[makeQuery(id+"F4.imprint","IMPRINT",EDGE,{"derivedFrom":subQ0}),-1.0]])]});}
            var Q31;
            {var subQ0=sQuery(id+"F4.wireOp",EDGE,"E51");Q31=makeQuery(id+"F4.imprint","IMPRINT",FACE,{"disambiguationData":[TD([[makeQuery(id+"F4.imprint","IMPRINT",EDGE,{"derivedFrom":subQ0}),1.0]])]});}
            extrude(context, id + "F5", {"entities" : qUnion([Q0, Q1, Q2, Q3, Q4, Q5, Q6, Q7, Q8, Q9, Q10, Q11, Q12, Q13, Q14, Q15, Q16, Q17, Q18, Q19, Q20, Q21, Q22, Q23, Q24, Q25, Q26, Q27, Q28, Q29, Q30, Q31]), "operationType" : NewBodyOperationType.REMOVE, "oppositeDirection" : true, "depth" : 5 * mm, "offsetDistance" : 25 * mm});
        }
        {
            var Q0;
            Q0=makeQuery(id+"F1.opExtrude","SWEPT_FACE",FACE,{"disambiguationData":[OSD([sQuery(id+"F0.wireOp",EDGE,"E0.top")])]});
            var sketch = newSketch(context, id + "F6", { "sketchPlane" : qUnion([Q0])});
            skLineSegment(sketch, "E93.0", {"start": v(-119.44, 9.48) * mm, "end": v(-9.44, 9.48) * mm});
            skLineSegment(sketch, "E93.1", {"start": v(-119.44, 149.48) * mm, "end": v(-119.44, 9.48) * mm});
            skLineSegment(sketch, "E93.2", {"start": v(-9.44, 149.48) * mm, "end": v(-119.44, 149.48) * mm});
            skLineSegment(sketch, "E93.3", {"start": v(-9.44, 9.48) * mm, "end": v(-9.44, 149.48) * mm});
            skLineSegment(sketch, "E94", {"start": v(-119.44, 79.48) * mm, "end": v(-9.44, 79.48) * mm});
            skLineSegment(sketch, "E95.0", {"start": v(-119.44, 74.48) * mm, "end": v(-9.44, 74.48) * mm});
            skLineSegment(sketch, "E96.0", {"start": v(-119.44, 84.48) * mm, "end": v(-9.44, 84.48) * mm});
            skLineSegment(sketch, "E97", {"start": v(-119.44, 84.48) * mm, "end": v(-69.44, 149.48) * mm});
            skLineSegment(sketch, "E98", {"start": v(-64.44, 140.53) * mm, "end": v(-84.54, 112.63) * mm});
            skLineSegment(sketch, "E99", {"start": v(-84.54, 112.63) * mm, "end": v(-80.92, 103.88) * mm});
            skLineSegment(sketch, "E100", {"start": v(-80.92, 103.88) * mm, "end": v(-64.44, 126.95) * mm});
            skLineSegment(sketch, "E101", {"start": v(-82.43, 79.48) * mm, "end": v(-100.67, 79.48) * mm});
            skLineSegment(sketch, "E102", {"start": v(-91.55, 79.48) * mm, "end": v(-91.55, 101.32) * mm});
            skLineSegment(sketch, "E103", {"start": v(-91.55, 101.32) * mm, "end": v(-100.67, 79.48) * mm});
            skLineSegment(sketch, "E104", {"start": v(-91.55, 101.32) * mm, "end": v(-82.43, 79.48) * mm});
            skLineSegment(sketch, "E105", {"start": v(-64.44, 79.48) * mm, "end": v(-64.44, 101.32) * mm});
            skLineSegment(sketch, "E106", {"start": v(-64.44, 101.32) * mm, "end": v(-72.93, 79.48) * mm});
            skLineSegment(sketch, "E107.MirrorCS", {"start": v(-64.44, 140.53) * mm, "end": v(-44.34, 112.63) * mm});
            skLineSegment(sketch, "E108.MirrorCS", {"start": v(-47.96, 103.88) * mm, "end": v(-64.44, 126.95) * mm});
            skLineSegment(sketch, "E109.MirrorCS", {"start": v(-44.34, 112.63) * mm, "end": v(-47.96, 103.88) * mm});
            skLineSegment(sketch, "E110.MirrorCS", {"start": v(-9.44, 84.48) * mm, "end": v(-59.44, 149.48) * mm});
            skLineSegment(sketch, "E111.MirrorCS", {"start": v(-37.33, 101.32) * mm, "end": v(-46.45, 79.48) * mm});
            skLineSegment(sketch, "E112.MirrorCS", {"start": v(-37.33, 79.48) * mm, "end": v(-37.33, 101.32) * mm});
            skLineSegment(sketch, "E113.MirrorCS", {"start": v(-37.33, 101.32) * mm, "end": v(-28.2, 79.48) * mm});
            skLineSegment(sketch, "E114.MirrorCS", {"start": v(-64.44, 101.32) * mm, "end": v(-55.95, 79.48) * mm});
            skLineSegment(sketch, "E115.MirrorCS", {"start": v(-9.44, 74.48) * mm, "end": v(-59.44, 9.48) * mm});
            skLineSegment(sketch, "E116.MirrorCS", {"start": v(-37.33, 57.65) * mm, "end": v(-28.2, 79.48) * mm});
            skLineSegment(sketch, "E117.MirrorCS", {"start": v(-37.33, 79.48) * mm, "end": v(-37.33, 57.65) * mm});
            skLineSegment(sketch, "E118.MirrorCS", {"start": v(-37.33, 57.65) * mm, "end": v(-46.45, 79.48) * mm});
            skLineSegment(sketch, "E119.MirrorCS", {"start": v(-47.96, 55.08) * mm, "end": v(-64.44, 32.01) * mm});
            skLineSegment(sketch, "E120.MirrorCS", {"start": v(-44.34, 46.34) * mm, "end": v(-47.96, 55.08) * mm});
            skLineSegment(sketch, "E121.MirrorCS", {"start": v(-64.44, 18.44) * mm, "end": v(-44.34, 46.34) * mm});
            skLineSegment(sketch, "E122.MirrorCS", {"start": v(-64.44, 18.44) * mm, "end": v(-84.54, 46.34) * mm});
            skLineSegment(sketch, "E123.MirrorCS", {"start": v(-80.92, 55.08) * mm, "end": v(-64.44, 32.01) * mm});
            skLineSegment(sketch, "E124.MirrorCS", {"start": v(-84.54, 46.34) * mm, "end": v(-80.92, 55.08) * mm});
            skLineSegment(sketch, "E125.MirrorCS", {"start": v(-64.44, 57.65) * mm, "end": v(-72.93, 79.48) * mm});
            skLineSegment(sketch, "E126.MirrorCS", {"start": v(-64.44, 57.65) * mm, "end": v(-55.95, 79.48) * mm});
            skLineSegment(sketch, "E127.MirrorCS", {"start": v(-91.55, 57.65) * mm, "end": v(-82.43, 79.48) * mm});
            skLineSegment(sketch, "E128.MirrorCS", {"start": v(-91.55, 57.65) * mm, "end": v(-100.67, 79.48) * mm});
            skLineSegment(sketch, "E129.MirrorCS", {"start": v(-119.44, 74.48) * mm, "end": v(-69.44, 9.48) * mm});
            skLineSegment(sketch, "E130", {"start": v(-119.44, 149.48) * mm, "end": v(-119.44, 84.48) * mm});
            skLineSegment(sketch, "E131", {"start": v(-119.44, 149.48) * mm, "end": v(-9.44, 149.48) * mm});
            skLineSegment(sketch, "E132", {"start": v(-9.44, 149.48) * mm, "end": v(-9.44, 9.48) * mm});
            skLineSegment(sketch, "E133", {"start": v(-9.44, 9.48) * mm, "end": v(-119.44, 9.48) * mm});
            skLineSegment(sketch, "E134", {"start": v(-119.44, 9.48) * mm, "end": v(-119.44, 74.48) * mm});
            skLineSegment(sketch, "E135.trimOffspring", {"start": v(-69.44, 88.46) * mm, "end": v(-69.44, 70.5) * mm});
            skLineSegment(sketch, "E136.trimOffspring", {"start": v(-64.44, 101.32) * mm, "end": v(-64.44, 57.65) * mm});
            skLineSegment(sketch, "E137.trimOffspring", {"start": v(-64.44, 18.44) * mm, "end": v(-64.44, 9.48) * mm});
            skPoint(sketch, "E138.start.orphan", {"position": v(-64.44, 149.48) * mm});
            skSolve(sketch);
        }
        {
            var Q0;
            {var subQ0=sQuery(id+"F6.wireOp",EDGE,"E97");Q0=makeQuery(id+"F6.imprint","IMPRINT",FACE,{"disambiguationData":[TD([[makeQuery(id+"F6.imprint","IMPRINT",EDGE,{"derivedFrom":subQ0}),1.0]])]});}
            var Q1;
            {var subQ0=sQuery(id+"F6.wireOp",EDGE,"E110.MirrorCS");Q1=makeQuery(id+"F6.imprint","IMPRINT",FACE,{"disambiguationData":[TD([[makeQuery(id+"F6.imprint","IMPRINT",EDGE,{"derivedFrom":subQ0}),-1.0]])]});}
            var Q2;
            Q2=makeQuery(id+"F6.imprint","IMPRINT",FACE,{"disambiguationData":[TD([[makeQuery(id+"F6.imprint","IMPRINT",EDGE,{"derivedFrom":sQuery(id+"F6.wireOp",EDGE,"E98")}),1.0]])]});
            var Q3;
            {var subQ0=sQuery(id+"F6.wireOp",EDGE,"E112.MirrorCS");var subQ1=sQuery(id+"F6.wireOp",EDGE,"E96.0");var subQ2=makeQuery(id+"F6.imprint","INTERSECT",VERTEX,{"derivedFrom":[subQ1,subQ0]});Q3=makeQuery(id+"F6.imprint","IMPRINT",FACE,{"disambiguationData":[TD([[makeQuery(id+"F6.imprint","IMPRINT",EDGE,{"disambiguationData":[TD([[subQ2,-1.0]])],"derivedFrom":subQ1}),1.0]])]});}
            var Q4;
            {var subQ0=sQuery(id+"F6.wireOp",EDGE,"E111.MirrorCS");var subQ1=sQuery(id+"F6.wireOp",EDGE,"E96.0");var subQ2=makeQuery(id+"F6.imprint","INTERSECT",VERTEX,{"derivedFrom":[subQ1,subQ0]});Q4=makeQuery(id+"F6.imprint","IMPRINT",FACE,{"disambiguationData":[TD([[makeQuery(id+"F6.imprint","IMPRINT",EDGE,{"disambiguationData":[TD([[subQ2,-1.0]])],"derivedFrom":subQ1}),1.0]])]});}
            var Q5;
            {var subQ0=sQuery(id+"F6.wireOp",EDGE,"E111.MirrorCS");var subQ5=sQuery(id+"F6.wireOp",EDGE,"E96.0");var subQ6=makeQuery(id+"F6.imprint","INTERSECT",VERTEX,{"derivedFrom":[subQ5,subQ0]});Q5=makeQuery(id+"F6.imprint","IMPRINT",FACE,{"disambiguationData":[TD([[makeQuery(id+"F6.imprint","IMPRINT",EDGE,{"disambiguationData":[TD([[subQ6,-1.0]])],"derivedFrom":subQ5}),-1.0]])]});}
            var Q6;
            {var subQ3=sQuery(id+"F6.wireOp",EDGE,"E112.MirrorCS");var subQ5=sQuery(id+"F6.wireOp",EDGE,"E96.0");var subQ7=makeQuery(id+"F6.imprint","INTERSECT",VERTEX,{"derivedFrom":[subQ5,subQ3]});Q6=makeQuery(id+"F6.imprint","IMPRINT",FACE,{"disambiguationData":[TD([[makeQuery(id+"F6.imprint","IMPRINT",EDGE,{"disambiguationData":[TD([[subQ7,-1.0]])],"derivedFrom":subQ5}),-1.0]])]});}
            var Q7;
            {var subQ3=sQuery(id+"F6.wireOp",EDGE,"E117.MirrorCS");var subQ5=sQuery(id+"F6.wireOp",EDGE,"E95.0");var subQ6=makeQuery(id+"F6.imprint","INTERSECT",VERTEX,{"derivedFrom":[subQ5,subQ3]});Q7=makeQuery(id+"F6.imprint","IMPRINT",FACE,{"disambiguationData":[TD([[makeQuery(id+"F6.imprint","IMPRINT",EDGE,{"disambiguationData":[TD([[subQ6,-1.0]])],"derivedFrom":subQ5}),1.0]])]});}
            var Q8;
            {var subQ0=sQuery(id+"F6.wireOp",EDGE,"E118.MirrorCS");var subQ5=sQuery(id+"F6.wireOp",EDGE,"E95.0");var subQ6=makeQuery(id+"F6.imprint","INTERSECT",VERTEX,{"derivedFrom":[subQ5,subQ0]});Q8=makeQuery(id+"F6.imprint","IMPRINT",FACE,{"disambiguationData":[TD([[makeQuery(id+"F6.imprint","IMPRINT",EDGE,{"disambiguationData":[TD([[subQ6,-1.0]])],"derivedFrom":subQ5}),1.0]])]});}
            var Q9;
            {var subQ0=sQuery(id+"F6.wireOp",EDGE,"E118.MirrorCS");var subQ1=sQuery(id+"F6.wireOp",EDGE,"E95.0");var subQ2=makeQuery(id+"F6.imprint","INTERSECT",VERTEX,{"derivedFrom":[subQ1,subQ0]});Q9=makeQuery(id+"F6.imprint","IMPRINT",FACE,{"disambiguationData":[TD([[makeQuery(id+"F6.imprint","IMPRINT",EDGE,{"disambiguationData":[TD([[subQ2,-1.0]])],"derivedFrom":subQ1}),-1.0]])]});}
            var Q10;
            {var subQ0=sQuery(id+"F6.wireOp",EDGE,"E117.MirrorCS");var subQ1=sQuery(id+"F6.wireOp",EDGE,"E95.0");var subQ2=makeQuery(id+"F6.imprint","INTERSECT",VERTEX,{"derivedFrom":[subQ1,subQ0]});Q10=makeQuery(id+"F6.imprint","IMPRINT",FACE,{"disambiguationData":[TD([[makeQuery(id+"F6.imprint","IMPRINT",EDGE,{"disambiguationData":[TD([[subQ2,-1.0]])],"derivedFrom":subQ1}),-1.0]])]});}
            var Q11;
            {var subQ0=sQuery(id+"F6.wireOp",EDGE,"E136.trimOffspring");var subQ1=sQuery(id+"F6.wireOp",EDGE,"E96.0");var subQ2=makeQuery(id+"F6.imprint","INTERSECT",VERTEX,{"derivedFrom":[subQ1,subQ0]});Q11=makeQuery(id+"F6.imprint","IMPRINT",FACE,{"disambiguationData":[TD([[makeQuery(id+"F6.imprint","IMPRINT",EDGE,{"disambiguationData":[TD([[subQ2,-1.0]])],"derivedFrom":subQ1}),1.0]])]});}
            var Q12;
            {var subQ0=sQuery(id+"F6.wireOp",EDGE,"E135.trimOffspring");var subQ1=sQuery(id+"F6.wireOp",EDGE,"E96.0");var subQ2=makeQuery(id+"F6.imprint","INTERSECT",VERTEX,{"derivedFrom":[subQ1,subQ0]});Q12=makeQuery(id+"F6.imprint","IMPRINT",FACE,{"disambiguationData":[TD([[makeQuery(id+"F6.imprint","IMPRINT",EDGE,{"disambiguationData":[TD([[subQ2,-1.0]])],"derivedFrom":subQ1}),1.0]])]});}
            var Q13;
            {var subQ0=sQuery(id+"F6.wireOp",EDGE,"E106");var subQ1=sQuery(id+"F6.wireOp",EDGE,"E96.0");var subQ2=makeQuery(id+"F6.imprint","INTERSECT",VERTEX,{"derivedFrom":[subQ1,subQ0]});Q13=makeQuery(id+"F6.imprint","IMPRINT",FACE,{"disambiguationData":[TD([[makeQuery(id+"F6.imprint","IMPRINT",EDGE,{"disambiguationData":[TD([[subQ2,-1.0]])],"derivedFrom":subQ1}),1.0]])]});}
            var Q14;
            {var subQ0=sQuery(id+"F6.wireOp",EDGE,"E106");var subQ5=sQuery(id+"F6.wireOp",EDGE,"E96.0");var subQ6=makeQuery(id+"F6.imprint","INTERSECT",VERTEX,{"derivedFrom":[subQ5,subQ0]});Q14=makeQuery(id+"F6.imprint","IMPRINT",FACE,{"disambiguationData":[TD([[makeQuery(id+"F6.imprint","IMPRINT",EDGE,{"disambiguationData":[TD([[subQ6,-1.0]])],"derivedFrom":subQ5}),-1.0]])]});}
            var Q15;
            {var subQ0=sQuery(id+"F6.wireOp",EDGE,"E135.trimOffspring");var subQ1=sQuery(id+"F6.wireOp",EDGE,"E94");var subQ2=makeQuery(id+"F6.imprint","INTERSECT",VERTEX,{"derivedFrom":[subQ1,subQ0]});Q15=makeQuery(id+"F6.imprint","IMPRINT",FACE,{"disambiguationData":[TD([[makeQuery(id+"F6.imprint","IMPRINT",EDGE,{"disambiguationData":[TD([[subQ2,-1.0]])],"derivedFrom":subQ1}),1.0]])]});}
            var Q16;
            {var subQ3=sQuery(id+"F6.wireOp",EDGE,"E136.trimOffspring");var subQ5=sQuery(id+"F6.wireOp",EDGE,"E96.0");var subQ6=makeQuery(id+"F6.imprint","INTERSECT",VERTEX,{"derivedFrom":[subQ5,subQ3]});Q16=makeQuery(id+"F6.imprint","IMPRINT",FACE,{"disambiguationData":[TD([[makeQuery(id+"F6.imprint","IMPRINT",EDGE,{"disambiguationData":[TD([[subQ6,-1.0]])],"derivedFrom":subQ5}),-1.0]])]});}
            var Q17;
            {var subQ3=sQuery(id+"F6.wireOp",EDGE,"E136.trimOffspring");var subQ5=sQuery(id+"F6.wireOp",EDGE,"E95.0");var subQ6=makeQuery(id+"F6.imprint","INTERSECT",VERTEX,{"derivedFrom":[subQ5,subQ3]});Q17=makeQuery(id+"F6.imprint","IMPRINT",FACE,{"disambiguationData":[TD([[makeQuery(id+"F6.imprint","IMPRINT",EDGE,{"disambiguationData":[TD([[subQ6,-1.0]])],"derivedFrom":subQ5}),1.0]])]});}
            var Q18;
            {var subQ0=sQuery(id+"F6.wireOp",EDGE,"E135.trimOffspring");var subQ1=sQuery(id+"F6.wireOp",EDGE,"E94");var subQ2=makeQuery(id+"F6.imprint","INTERSECT",VERTEX,{"derivedFrom":[subQ1,subQ0]});Q18=makeQuery(id+"F6.imprint","IMPRINT",FACE,{"disambiguationData":[TD([[makeQuery(id+"F6.imprint","IMPRINT",EDGE,{"disambiguationData":[TD([[subQ2,-1.0]])],"derivedFrom":subQ1}),-1.0]])]});}
            var Q19;
            {var subQ0=sQuery(id+"F6.wireOp",EDGE,"E125.MirrorCS");var subQ5=sQuery(id+"F6.wireOp",EDGE,"E95.0");var subQ6=makeQuery(id+"F6.imprint","INTERSECT",VERTEX,{"derivedFrom":[subQ5,subQ0]});Q19=makeQuery(id+"F6.imprint","IMPRINT",FACE,{"disambiguationData":[TD([[makeQuery(id+"F6.imprint","IMPRINT",EDGE,{"disambiguationData":[TD([[subQ6,-1.0]])],"derivedFrom":subQ5}),1.0]])]});}
            var Q20;
            {var subQ0=sQuery(id+"F6.wireOp",EDGE,"E125.MirrorCS");var subQ1=sQuery(id+"F6.wireOp",EDGE,"E95.0");var subQ2=makeQuery(id+"F6.imprint","INTERSECT",VERTEX,{"derivedFrom":[subQ1,subQ0]});Q20=makeQuery(id+"F6.imprint","IMPRINT",FACE,{"disambiguationData":[TD([[makeQuery(id+"F6.imprint","IMPRINT",EDGE,{"disambiguationData":[TD([[subQ2,-1.0]])],"derivedFrom":subQ1}),-1.0]])]});}
            var Q21;
            {var subQ0=sQuery(id+"F6.wireOp",EDGE,"E135.trimOffspring");var subQ1=sQuery(id+"F6.wireOp",EDGE,"E95.0");var subQ2=makeQuery(id+"F6.imprint","INTERSECT",VERTEX,{"derivedFrom":[subQ1,subQ0]});Q21=makeQuery(id+"F6.imprint","IMPRINT",FACE,{"disambiguationData":[TD([[makeQuery(id+"F6.imprint","IMPRINT",EDGE,{"disambiguationData":[TD([[subQ2,-1.0]])],"derivedFrom":subQ1}),-1.0]])]});}
            var Q22;
            {var subQ0=sQuery(id+"F6.wireOp",EDGE,"E136.trimOffspring");var subQ1=sQuery(id+"F6.wireOp",EDGE,"E95.0");var subQ2=makeQuery(id+"F6.imprint","INTERSECT",VERTEX,{"derivedFrom":[subQ1,subQ0]});Q22=makeQuery(id+"F6.imprint","IMPRINT",FACE,{"disambiguationData":[TD([[makeQuery(id+"F6.imprint","IMPRINT",EDGE,{"disambiguationData":[TD([[subQ2,-1.0]])],"derivedFrom":subQ1}),-1.0]])]});}
            var Q23;
            {var subQ0=sQuery(id+"F6.wireOp",EDGE,"E102");var subQ1=sQuery(id+"F6.wireOp",EDGE,"E96.0");var subQ2=makeQuery(id+"F6.imprint","INTERSECT",VERTEX,{"derivedFrom":[subQ1,subQ0]});Q23=makeQuery(id+"F6.imprint","IMPRINT",FACE,{"disambiguationData":[TD([[makeQuery(id+"F6.imprint","IMPRINT",EDGE,{"disambiguationData":[TD([[subQ2,-1.0]])],"derivedFrom":subQ1}),1.0]])]});}
            var Q24;
            {var subQ0=sQuery(id+"F6.wireOp",EDGE,"E103");var subQ1=sQuery(id+"F6.wireOp",EDGE,"E96.0");var subQ2=makeQuery(id+"F6.imprint","INTERSECT",VERTEX,{"derivedFrom":[subQ1,subQ0]});Q24=makeQuery(id+"F6.imprint","IMPRINT",FACE,{"disambiguationData":[TD([[makeQuery(id+"F6.imprint","IMPRINT",EDGE,{"disambiguationData":[TD([[subQ2,-1.0]])],"derivedFrom":subQ1}),1.0]])]});}
            var Q25;
            {var subQ0=sQuery(id+"F6.wireOp",EDGE,"E103");var subQ1=sQuery(id+"F6.wireOp",EDGE,"E96.0");var subQ2=makeQuery(id+"F6.imprint","INTERSECT",VERTEX,{"derivedFrom":[subQ1,subQ0]});Q25=makeQuery(id+"F6.imprint","IMPRINT",FACE,{"disambiguationData":[TD([[makeQuery(id+"F6.imprint","IMPRINT",EDGE,{"disambiguationData":[TD([[subQ2,-1.0]])],"derivedFrom":subQ1}),-1.0]])]});}
            var Q26;
            {var subQ0=sQuery(id+"F6.wireOp",EDGE,"E102");var subQ1=sQuery(id+"F6.wireOp",EDGE,"E96.0");var subQ2=makeQuery(id+"F6.imprint","INTERSECT",VERTEX,{"derivedFrom":[subQ1,subQ0]});Q26=makeQuery(id+"F6.imprint","IMPRINT",FACE,{"disambiguationData":[TD([[makeQuery(id+"F6.imprint","IMPRINT",EDGE,{"disambiguationData":[TD([[subQ2,-1.0]])],"derivedFrom":subQ1}),-1.0]])]});}
            var Q27;
            {var subQ4=sQuery(id+"F6.wireOp",EDGE,"E95.0");var subQ6=sQuery(id+"F6.wireOp",EDGE,"E128.MirrorCS");var subQ7=makeQuery(id+"F6.imprint","INTERSECT",VERTEX,{"derivedFrom":[subQ4,subQ6]});Q27=makeQuery(id+"F6.imprint","IMPRINT",FACE,{"disambiguationData":[TD([[makeQuery(id+"F6.imprint","IMPRINT",EDGE,{"disambiguationData":[TD([[subQ7,-1.0]])],"derivedFrom":subQ4}),1.0]])]});}
            var Q28;
            {var subQ0=sQuery(id+"F6.wireOp",EDGE,"E128.MirrorCS");var subQ1=sQuery(id+"F6.wireOp",EDGE,"E95.0");var subQ2=makeQuery(id+"F6.imprint","INTERSECT",VERTEX,{"derivedFrom":[subQ1,subQ0]});Q28=makeQuery(id+"F6.imprint","IMPRINT",FACE,{"disambiguationData":[TD([[makeQuery(id+"F6.imprint","IMPRINT",EDGE,{"disambiguationData":[TD([[subQ2,-1.0]])],"derivedFrom":subQ1}),-1.0]])]});}
            var Q29;
            Q29=makeQuery(id+"F6.imprint","IMPRINT",FACE,{"disambiguationData":[TD([[makeQuery(id+"F6.imprint","IMPRINT",EDGE,{"derivedFrom":sQuery(id+"F6.wireOp",EDGE,"E119.MirrorCS")}),1.0]])]});
            var Q30;
            {var subQ0=sQuery(id+"F6.wireOp",EDGE,"E129.MirrorCS");Q30=makeQuery(id+"F6.imprint","IMPRINT",FACE,{"disambiguationData":[TD([[makeQuery(id+"F6.imprint","IMPRINT",EDGE,{"derivedFrom":subQ0}),-1.0]])]});}
            var Q31;
            {var subQ0=sQuery(id+"F6.wireOp",EDGE,"E115.MirrorCS");Q31=makeQuery(id+"F6.imprint","IMPRINT",FACE,{"disambiguationData":[TD([[makeQuery(id+"F6.imprint","IMPRINT",EDGE,{"derivedFrom":subQ0}),1.0]])]});}
            extrude(context, id + "F7", {"entities" : qUnion([Q0, Q1, Q2, Q3, Q4, Q5, Q6, Q7, Q8, Q9, Q10, Q11, Q12, Q13, Q14, Q15, Q16, Q17, Q18, Q19, Q20, Q21, Q22, Q23, Q24, Q25, Q26, Q27, Q28, Q29, Q30, Q31]), "operationType" : NewBodyOperationType.REMOVE, "oppositeDirection" : true, "depth" : 5 * mm, "offsetDistance" : 25 * mm});
        }
        {
            var Q0;
            Q0=makeQuery(id+"F1.opExtrude","SWEPT_FACE",FACE,{"disambiguationData":[OSD([sQuery(id+"F0.wireOp",EDGE,"E0.left")])]});
            var sketch = newSketch(context, id + "F8", { "sketchPlane" : qUnion([Q0])});
            skLineSegment(sketch, "E139.0", {"start": v(-119.44, 9.48) * mm, "end": v(-9.44, 9.48) * mm});
            skLineSegment(sketch, "E139.1", {"start": v(-119.44, 149.48) * mm, "end": v(-119.44, 9.48) * mm});
            skLineSegment(sketch, "E139.2", {"start": v(-9.44, 149.48) * mm, "end": v(-119.44, 149.48) * mm});
            skLineSegment(sketch, "E139.3", {"start": v(-9.44, 9.48) * mm, "end": v(-9.44, 149.48) * mm});
            skLineSegment(sketch, "E140", {"start": v(-119.44, 79.48) * mm, "end": v(-9.44, 79.48) * mm});
            skLineSegment(sketch, "E141.0", {"start": v(-119.44, 74.48) * mm, "end": v(-9.44, 74.48) * mm});
            skLineSegment(sketch, "E142.0", {"start": v(-119.44, 84.48) * mm, "end": v(-9.44, 84.48) * mm});
            skLineSegment(sketch, "E143", {"start": v(-119.44, 84.48) * mm, "end": v(-69.44, 149.48) * mm});
            skLineSegment(sketch, "E144", {"start": v(-64.44, 140.53) * mm, "end": v(-84.54, 112.63) * mm});
            skLineSegment(sketch, "E145", {"start": v(-84.54, 112.63) * mm, "end": v(-80.92, 103.88) * mm});
            skLineSegment(sketch, "E146", {"start": v(-80.92, 103.88) * mm, "end": v(-64.44, 126.95) * mm});
            skLineSegment(sketch, "E147", {"start": v(-82.43, 79.48) * mm, "end": v(-100.67, 79.48) * mm});
            skLineSegment(sketch, "E148", {"start": v(-91.55, 79.48) * mm, "end": v(-91.55, 101.32) * mm});
            skLineSegment(sketch, "E149", {"start": v(-91.55, 101.32) * mm, "end": v(-100.67, 79.48) * mm});
            skLineSegment(sketch, "E150", {"start": v(-91.55, 101.32) * mm, "end": v(-82.43, 79.48) * mm});
            skLineSegment(sketch, "E151", {"start": v(-64.44, 79.48) * mm, "end": v(-64.44, 101.32) * mm});
            skLineSegment(sketch, "E152", {"start": v(-64.44, 101.32) * mm, "end": v(-72.93, 79.48) * mm});
            skLineSegment(sketch, "E153.MirrorCS", {"start": v(-64.44, 140.53) * mm, "end": v(-44.34, 112.63) * mm});
            skLineSegment(sketch, "E154.MirrorCS", {"start": v(-47.96, 103.88) * mm, "end": v(-64.44, 126.95) * mm});
            skLineSegment(sketch, "E155.MirrorCS", {"start": v(-44.34, 112.63) * mm, "end": v(-47.96, 103.88) * mm});
            skLineSegment(sketch, "E156.MirrorCS", {"start": v(-9.44, 84.48) * mm, "end": v(-59.44, 149.48) * mm});
            skLineSegment(sketch, "E157.MirrorCS", {"start": v(-37.33, 101.32) * mm, "end": v(-46.45, 79.48) * mm});
            skLineSegment(sketch, "E158.MirrorCS", {"start": v(-37.33, 79.48) * mm, "end": v(-37.33, 101.32) * mm});
            skLineSegment(sketch, "E159.MirrorCS", {"start": v(-37.33, 101.32) * mm, "end": v(-28.2, 79.48) * mm});
            skLineSegment(sketch, "E160.MirrorCS", {"start": v(-64.44, 101.32) * mm, "end": v(-55.95, 79.48) * mm});
            skLineSegment(sketch, "E161.MirrorCS", {"start": v(-9.44, 74.48) * mm, "end": v(-59.44, 9.48) * mm});
            skLineSegment(sketch, "E162.MirrorCS", {"start": v(-37.33, 57.65) * mm, "end": v(-28.2, 79.48) * mm});
            skLineSegment(sketch, "E163.MirrorCS", {"start": v(-37.33, 79.48) * mm, "end": v(-37.33, 57.65) * mm});
            skLineSegment(sketch, "E164.MirrorCS", {"start": v(-37.33, 57.65) * mm, "end": v(-46.45, 79.48) * mm});
            skLineSegment(sketch, "E165.MirrorCS", {"start": v(-47.96, 55.08) * mm, "end": v(-64.44, 32.01) * mm});
            skLineSegment(sketch, "E166.MirrorCS", {"start": v(-44.34, 46.34) * mm, "end": v(-47.96, 55.08) * mm});
            skLineSegment(sketch, "E167.MirrorCS", {"start": v(-64.44, 18.44) * mm, "end": v(-44.34, 46.34) * mm});
            skLineSegment(sketch, "E168.MirrorCS", {"start": v(-64.44, 18.44) * mm, "end": v(-84.54, 46.34) * mm});
            skLineSegment(sketch, "E169.MirrorCS", {"start": v(-80.92, 55.08) * mm, "end": v(-64.44, 32.01) * mm});
            skLineSegment(sketch, "E170.MirrorCS", {"start": v(-84.54, 46.34) * mm, "end": v(-80.92, 55.08) * mm});
            skLineSegment(sketch, "E171.MirrorCS", {"start": v(-64.44, 57.65) * mm, "end": v(-72.93, 79.48) * mm});
            skLineSegment(sketch, "E172.MirrorCS", {"start": v(-64.44, 57.65) * mm, "end": v(-55.95, 79.48) * mm});
            skLineSegment(sketch, "E173.MirrorCS", {"start": v(-91.55, 57.65) * mm, "end": v(-82.43, 79.48) * mm});
            skLineSegment(sketch, "E174.MirrorCS", {"start": v(-91.55, 57.65) * mm, "end": v(-100.67, 79.48) * mm});
            skLineSegment(sketch, "E175.MirrorCS", {"start": v(-119.44, 74.48) * mm, "end": v(-69.44, 9.48) * mm});
            skLineSegment(sketch, "E176", {"start": v(-119.44, 149.48) * mm, "end": v(-119.44, 84.48) * mm});
            skLineSegment(sketch, "E177", {"start": v(-119.44, 149.48) * mm, "end": v(-9.44, 149.48) * mm});
            skLineSegment(sketch, "E178", {"start": v(-9.44, 149.48) * mm, "end": v(-9.44, 9.48) * mm});
            skLineSegment(sketch, "E179", {"start": v(-9.44, 9.48) * mm, "end": v(-119.44, 9.48) * mm});
            skLineSegment(sketch, "E180", {"start": v(-119.44, 9.48) * mm, "end": v(-119.44, 74.48) * mm});
            skLineSegment(sketch, "E181.trimOffspring", {"start": v(-69.44, 88.46) * mm, "end": v(-69.44, 70.5) * mm});
            skLineSegment(sketch, "E182.trimOffspring", {"start": v(-64.44, 101.32) * mm, "end": v(-64.44, 57.65) * mm});
            skLineSegment(sketch, "E183.trimOffspring", {"start": v(-64.44, 18.44) * mm, "end": v(-64.44, 9.48) * mm});
            skPoint(sketch, "E184.start.orphan", {"position": v(-64.44, 149.48) * mm});
            skSolve(sketch);
        }
        {
            var Q0;
            {var subQ0=sQuery(id+"F8.wireOp",EDGE,"E156.MirrorCS");Q0=makeQuery(id+"F8.imprint","IMPRINT",FACE,{"disambiguationData":[TD([[makeQuery(id+"F8.imprint","IMPRINT",EDGE,{"derivedFrom":subQ0}),-1.0]])]});}
            var Q1;
            Q1=makeQuery(id+"F8.imprint","IMPRINT",FACE,{"disambiguationData":[TD([[makeQuery(id+"F8.imprint","IMPRINT",EDGE,{"derivedFrom":sQuery(id+"F8.wireOp",EDGE,"E144")}),1.0]])]});
            var Q2;
            {var subQ0=sQuery(id+"F8.wireOp",EDGE,"E143");Q2=makeQuery(id+"F8.imprint","IMPRINT",FACE,{"disambiguationData":[TD([[makeQuery(id+"F8.imprint","IMPRINT",EDGE,{"derivedFrom":subQ0}),1.0]])]});}
            var Q3;
            {var subQ0=sQuery(id+"F8.wireOp",EDGE,"E158.MirrorCS");var subQ1=sQuery(id+"F8.wireOp",EDGE,"E142.0");var subQ2=makeQuery(id+"F8.imprint","INTERSECT",VERTEX,{"derivedFrom":[subQ1,subQ0]});Q3=makeQuery(id+"F8.imprint","IMPRINT",FACE,{"disambiguationData":[TD([[makeQuery(id+"F8.imprint","IMPRINT",EDGE,{"disambiguationData":[TD([[subQ2,-1.0]])],"derivedFrom":subQ1}),1.0]])]});}
            var Q4;
            {var subQ0=sQuery(id+"F8.wireOp",EDGE,"E157.MirrorCS");var subQ1=sQuery(id+"F8.wireOp",EDGE,"E142.0");var subQ2=makeQuery(id+"F8.imprint","INTERSECT",VERTEX,{"derivedFrom":[subQ1,subQ0]});Q4=makeQuery(id+"F8.imprint","IMPRINT",FACE,{"disambiguationData":[TD([[makeQuery(id+"F8.imprint","IMPRINT",EDGE,{"disambiguationData":[TD([[subQ2,-1.0]])],"derivedFrom":subQ1}),1.0]])]});}
            var Q5;
            {var subQ0=sQuery(id+"F8.wireOp",EDGE,"E157.MirrorCS");var subQ5=sQuery(id+"F8.wireOp",EDGE,"E142.0");var subQ6=makeQuery(id+"F8.imprint","INTERSECT",VERTEX,{"derivedFrom":[subQ5,subQ0]});Q5=makeQuery(id+"F8.imprint","IMPRINT",FACE,{"disambiguationData":[TD([[makeQuery(id+"F8.imprint","IMPRINT",EDGE,{"disambiguationData":[TD([[subQ6,-1.0]])],"derivedFrom":subQ5}),-1.0]])]});}
            var Q6;
            {var subQ3=sQuery(id+"F8.wireOp",EDGE,"E158.MirrorCS");var subQ5=sQuery(id+"F8.wireOp",EDGE,"E142.0");var subQ7=makeQuery(id+"F8.imprint","INTERSECT",VERTEX,{"derivedFrom":[subQ5,subQ3]});Q6=makeQuery(id+"F8.imprint","IMPRINT",FACE,{"disambiguationData":[TD([[makeQuery(id+"F8.imprint","IMPRINT",EDGE,{"disambiguationData":[TD([[subQ7,-1.0]])],"derivedFrom":subQ5}),-1.0]])]});}
            var Q7;
            {var subQ3=sQuery(id+"F8.wireOp",EDGE,"E163.MirrorCS");var subQ5=sQuery(id+"F8.wireOp",EDGE,"E141.0");var subQ6=makeQuery(id+"F8.imprint","INTERSECT",VERTEX,{"derivedFrom":[subQ5,subQ3]});Q7=makeQuery(id+"F8.imprint","IMPRINT",FACE,{"disambiguationData":[TD([[makeQuery(id+"F8.imprint","IMPRINT",EDGE,{"disambiguationData":[TD([[subQ6,-1.0]])],"derivedFrom":subQ5}),1.0]])]});}
            var Q8;
            {var subQ0=sQuery(id+"F8.wireOp",EDGE,"E163.MirrorCS");var subQ1=sQuery(id+"F8.wireOp",EDGE,"E141.0");var subQ2=makeQuery(id+"F8.imprint","INTERSECT",VERTEX,{"derivedFrom":[subQ1,subQ0]});Q8=makeQuery(id+"F8.imprint","IMPRINT",FACE,{"disambiguationData":[TD([[makeQuery(id+"F8.imprint","IMPRINT",EDGE,{"disambiguationData":[TD([[subQ2,-1.0]])],"derivedFrom":subQ1}),-1.0]])]});}
            var Q9;
            {var subQ0=sQuery(id+"F8.wireOp",EDGE,"E164.MirrorCS");var subQ1=sQuery(id+"F8.wireOp",EDGE,"E141.0");var subQ2=makeQuery(id+"F8.imprint","INTERSECT",VERTEX,{"derivedFrom":[subQ1,subQ0]});Q9=makeQuery(id+"F8.imprint","IMPRINT",FACE,{"disambiguationData":[TD([[makeQuery(id+"F8.imprint","IMPRINT",EDGE,{"disambiguationData":[TD([[subQ2,-1.0]])],"derivedFrom":subQ1}),-1.0]])]});}
            var Q10;
            {var subQ0=sQuery(id+"F8.wireOp",EDGE,"E164.MirrorCS");var subQ5=sQuery(id+"F8.wireOp",EDGE,"E141.0");var subQ6=makeQuery(id+"F8.imprint","INTERSECT",VERTEX,{"derivedFrom":[subQ5,subQ0]});Q10=makeQuery(id+"F8.imprint","IMPRINT",FACE,{"disambiguationData":[TD([[makeQuery(id+"F8.imprint","IMPRINT",EDGE,{"disambiguationData":[TD([[subQ6,-1.0]])],"derivedFrom":subQ5}),1.0]])]});}
            var Q11;
            {var subQ0=sQuery(id+"F8.wireOp",EDGE,"E182.trimOffspring");var subQ1=sQuery(id+"F8.wireOp",EDGE,"E142.0");var subQ2=makeQuery(id+"F8.imprint","INTERSECT",VERTEX,{"derivedFrom":[subQ1,subQ0]});Q11=makeQuery(id+"F8.imprint","IMPRINT",FACE,{"disambiguationData":[TD([[makeQuery(id+"F8.imprint","IMPRINT",EDGE,{"disambiguationData":[TD([[subQ2,-1.0]])],"derivedFrom":subQ1}),1.0]])]});}
            var Q12;
            {var subQ0=sQuery(id+"F8.wireOp",EDGE,"E181.trimOffspring");var subQ1=sQuery(id+"F8.wireOp",EDGE,"E142.0");var subQ2=makeQuery(id+"F8.imprint","INTERSECT",VERTEX,{"derivedFrom":[subQ1,subQ0]});Q12=makeQuery(id+"F8.imprint","IMPRINT",FACE,{"disambiguationData":[TD([[makeQuery(id+"F8.imprint","IMPRINT",EDGE,{"disambiguationData":[TD([[subQ2,-1.0]])],"derivedFrom":subQ1}),1.0]])]});}
            var Q13;
            {var subQ0=sQuery(id+"F8.wireOp",EDGE,"E152");var subQ1=sQuery(id+"F8.wireOp",EDGE,"E142.0");var subQ2=makeQuery(id+"F8.imprint","INTERSECT",VERTEX,{"derivedFrom":[subQ1,subQ0]});Q13=makeQuery(id+"F8.imprint","IMPRINT",FACE,{"disambiguationData":[TD([[makeQuery(id+"F8.imprint","IMPRINT",EDGE,{"disambiguationData":[TD([[subQ2,-1.0]])],"derivedFrom":subQ1}),1.0]])]});}
            var Q14;
            {var subQ0=sQuery(id+"F8.wireOp",EDGE,"E152");var subQ5=sQuery(id+"F8.wireOp",EDGE,"E142.0");var subQ6=makeQuery(id+"F8.imprint","INTERSECT",VERTEX,{"derivedFrom":[subQ5,subQ0]});Q14=makeQuery(id+"F8.imprint","IMPRINT",FACE,{"disambiguationData":[TD([[makeQuery(id+"F8.imprint","IMPRINT",EDGE,{"disambiguationData":[TD([[subQ6,-1.0]])],"derivedFrom":subQ5}),-1.0]])]});}
            var Q15;
            {var subQ0=sQuery(id+"F8.wireOp",EDGE,"E181.trimOffspring");var subQ1=sQuery(id+"F8.wireOp",EDGE,"E140");var subQ2=makeQuery(id+"F8.imprint","INTERSECT",VERTEX,{"derivedFrom":[subQ1,subQ0]});Q15=makeQuery(id+"F8.imprint","IMPRINT",FACE,{"disambiguationData":[TD([[makeQuery(id+"F8.imprint","IMPRINT",EDGE,{"disambiguationData":[TD([[subQ2,-1.0]])],"derivedFrom":subQ1}),1.0]])]});}
            var Q16;
            {var subQ3=sQuery(id+"F8.wireOp",EDGE,"E182.trimOffspring");var subQ5=sQuery(id+"F8.wireOp",EDGE,"E142.0");var subQ6=makeQuery(id+"F8.imprint","INTERSECT",VERTEX,{"derivedFrom":[subQ5,subQ3]});Q16=makeQuery(id+"F8.imprint","IMPRINT",FACE,{"disambiguationData":[TD([[makeQuery(id+"F8.imprint","IMPRINT",EDGE,{"disambiguationData":[TD([[subQ6,-1.0]])],"derivedFrom":subQ5}),-1.0]])]});}
            var Q17;
            {var subQ3=sQuery(id+"F8.wireOp",EDGE,"E182.trimOffspring");var subQ5=sQuery(id+"F8.wireOp",EDGE,"E141.0");var subQ6=makeQuery(id+"F8.imprint","INTERSECT",VERTEX,{"derivedFrom":[subQ5,subQ3]});Q17=makeQuery(id+"F8.imprint","IMPRINT",FACE,{"disambiguationData":[TD([[makeQuery(id+"F8.imprint","IMPRINT",EDGE,{"disambiguationData":[TD([[subQ6,-1.0]])],"derivedFrom":subQ5}),1.0]])]});}
            var Q18;
            {var subQ0=sQuery(id+"F8.wireOp",EDGE,"E181.trimOffspring");var subQ1=sQuery(id+"F8.wireOp",EDGE,"E140");var subQ2=makeQuery(id+"F8.imprint","INTERSECT",VERTEX,{"derivedFrom":[subQ1,subQ0]});Q18=makeQuery(id+"F8.imprint","IMPRINT",FACE,{"disambiguationData":[TD([[makeQuery(id+"F8.imprint","IMPRINT",EDGE,{"disambiguationData":[TD([[subQ2,-1.0]])],"derivedFrom":subQ1}),-1.0]])]});}
            var Q19;
            {var subQ0=sQuery(id+"F8.wireOp",EDGE,"E171.MirrorCS");var subQ5=sQuery(id+"F8.wireOp",EDGE,"E141.0");var subQ6=makeQuery(id+"F8.imprint","INTERSECT",VERTEX,{"derivedFrom":[subQ5,subQ0]});Q19=makeQuery(id+"F8.imprint","IMPRINT",FACE,{"disambiguationData":[TD([[makeQuery(id+"F8.imprint","IMPRINT",EDGE,{"disambiguationData":[TD([[subQ6,-1.0]])],"derivedFrom":subQ5}),1.0]])]});}
            var Q20;
            {var subQ0=sQuery(id+"F8.wireOp",EDGE,"E171.MirrorCS");var subQ1=sQuery(id+"F8.wireOp",EDGE,"E141.0");var subQ2=makeQuery(id+"F8.imprint","INTERSECT",VERTEX,{"derivedFrom":[subQ1,subQ0]});Q20=makeQuery(id+"F8.imprint","IMPRINT",FACE,{"disambiguationData":[TD([[makeQuery(id+"F8.imprint","IMPRINT",EDGE,{"disambiguationData":[TD([[subQ2,-1.0]])],"derivedFrom":subQ1}),-1.0]])]});}
            var Q21;
            {var subQ0=sQuery(id+"F8.wireOp",EDGE,"E181.trimOffspring");var subQ1=sQuery(id+"F8.wireOp",EDGE,"E141.0");var subQ2=makeQuery(id+"F8.imprint","INTERSECT",VERTEX,{"derivedFrom":[subQ1,subQ0]});Q21=makeQuery(id+"F8.imprint","IMPRINT",FACE,{"disambiguationData":[TD([[makeQuery(id+"F8.imprint","IMPRINT",EDGE,{"disambiguationData":[TD([[subQ2,-1.0]])],"derivedFrom":subQ1}),-1.0]])]});}
            var Q22;
            {var subQ0=sQuery(id+"F8.wireOp",EDGE,"E182.trimOffspring");var subQ1=sQuery(id+"F8.wireOp",EDGE,"E141.0");var subQ2=makeQuery(id+"F8.imprint","INTERSECT",VERTEX,{"derivedFrom":[subQ1,subQ0]});Q22=makeQuery(id+"F8.imprint","IMPRINT",FACE,{"disambiguationData":[TD([[makeQuery(id+"F8.imprint","IMPRINT",EDGE,{"disambiguationData":[TD([[subQ2,-1.0]])],"derivedFrom":subQ1}),-1.0]])]});}
            var Q23;
            {var subQ0=sQuery(id+"F8.wireOp",EDGE,"E174.MirrorCS");var subQ1=sQuery(id+"F8.wireOp",EDGE,"E141.0");var subQ2=makeQuery(id+"F8.imprint","INTERSECT",VERTEX,{"derivedFrom":[subQ1,subQ0]});Q23=makeQuery(id+"F8.imprint","IMPRINT",FACE,{"disambiguationData":[TD([[makeQuery(id+"F8.imprint","IMPRINT",EDGE,{"disambiguationData":[TD([[subQ2,-1.0]])],"derivedFrom":subQ1}),-1.0]])]});}
            var Q24;
            {var subQ4=sQuery(id+"F8.wireOp",EDGE,"E141.0");var subQ6=sQuery(id+"F8.wireOp",EDGE,"E174.MirrorCS");var subQ7=makeQuery(id+"F8.imprint","INTERSECT",VERTEX,{"derivedFrom":[subQ4,subQ6]});Q24=makeQuery(id+"F8.imprint","IMPRINT",FACE,{"disambiguationData":[TD([[makeQuery(id+"F8.imprint","IMPRINT",EDGE,{"disambiguationData":[TD([[subQ7,-1.0]])],"derivedFrom":subQ4}),1.0]])]});}
            var Q25;
            {var subQ0=sQuery(id+"F8.wireOp",EDGE,"E148");var subQ1=sQuery(id+"F8.wireOp",EDGE,"E142.0");var subQ2=makeQuery(id+"F8.imprint","INTERSECT",VERTEX,{"derivedFrom":[subQ1,subQ0]});Q25=makeQuery(id+"F8.imprint","IMPRINT",FACE,{"disambiguationData":[TD([[makeQuery(id+"F8.imprint","IMPRINT",EDGE,{"disambiguationData":[TD([[subQ2,-1.0]])],"derivedFrom":subQ1}),-1.0]])]});}
            var Q26;
            {var subQ0=sQuery(id+"F8.wireOp",EDGE,"E149");var subQ1=sQuery(id+"F8.wireOp",EDGE,"E142.0");var subQ2=makeQuery(id+"F8.imprint","INTERSECT",VERTEX,{"derivedFrom":[subQ1,subQ0]});Q26=makeQuery(id+"F8.imprint","IMPRINT",FACE,{"disambiguationData":[TD([[makeQuery(id+"F8.imprint","IMPRINT",EDGE,{"disambiguationData":[TD([[subQ2,-1.0]])],"derivedFrom":subQ1}),-1.0]])]});}
            var Q27;
            {var subQ0=sQuery(id+"F8.wireOp",EDGE,"E149");var subQ1=sQuery(id+"F8.wireOp",EDGE,"E142.0");var subQ2=makeQuery(id+"F8.imprint","INTERSECT",VERTEX,{"derivedFrom":[subQ1,subQ0]});Q27=makeQuery(id+"F8.imprint","IMPRINT",FACE,{"disambiguationData":[TD([[makeQuery(id+"F8.imprint","IMPRINT",EDGE,{"disambiguationData":[TD([[subQ2,-1.0]])],"derivedFrom":subQ1}),1.0]])]});}
            var Q28;
            {var subQ0=sQuery(id+"F8.wireOp",EDGE,"E148");var subQ1=sQuery(id+"F8.wireOp",EDGE,"E142.0");var subQ2=makeQuery(id+"F8.imprint","INTERSECT",VERTEX,{"derivedFrom":[subQ1,subQ0]});Q28=makeQuery(id+"F8.imprint","IMPRINT",FACE,{"disambiguationData":[TD([[makeQuery(id+"F8.imprint","IMPRINT",EDGE,{"disambiguationData":[TD([[subQ2,-1.0]])],"derivedFrom":subQ1}),1.0]])]});}
            var Q29;
            Q29=makeQuery(id+"F8.imprint","IMPRINT",FACE,{"disambiguationData":[TD([[makeQuery(id+"F8.imprint","IMPRINT",EDGE,{"derivedFrom":sQuery(id+"F8.wireOp",EDGE,"E165.MirrorCS")}),1.0]])]});
            var Q30;
            {var subQ0=sQuery(id+"F8.wireOp",EDGE,"E161.MirrorCS");Q30=makeQuery(id+"F8.imprint","IMPRINT",FACE,{"disambiguationData":[TD([[makeQuery(id+"F8.imprint","IMPRINT",EDGE,{"derivedFrom":subQ0}),1.0]])]});}
            var Q31;
            {var subQ0=sQuery(id+"F8.wireOp",EDGE,"E175.MirrorCS");Q31=makeQuery(id+"F8.imprint","IMPRINT",FACE,{"disambiguationData":[TD([[makeQuery(id+"F8.imprint","IMPRINT",EDGE,{"derivedFrom":subQ0}),-1.0]])]});}
            extrude(context, id + "F9", {"entities" : qUnion([Q0, Q1, Q2, Q3, Q4, Q5, Q6, Q7, Q8, Q9, Q10, Q11, Q12, Q13, Q14, Q15, Q16, Q17, Q18, Q19, Q20, Q21, Q22, Q23, Q24, Q25, Q26, Q27, Q28, Q29, Q30, Q31]), "operationType" : NewBodyOperationType.REMOVE, "oppositeDirection" : true, "depth" : 5 * mm, "offsetDistance" : 25 * mm});
        }
    });
